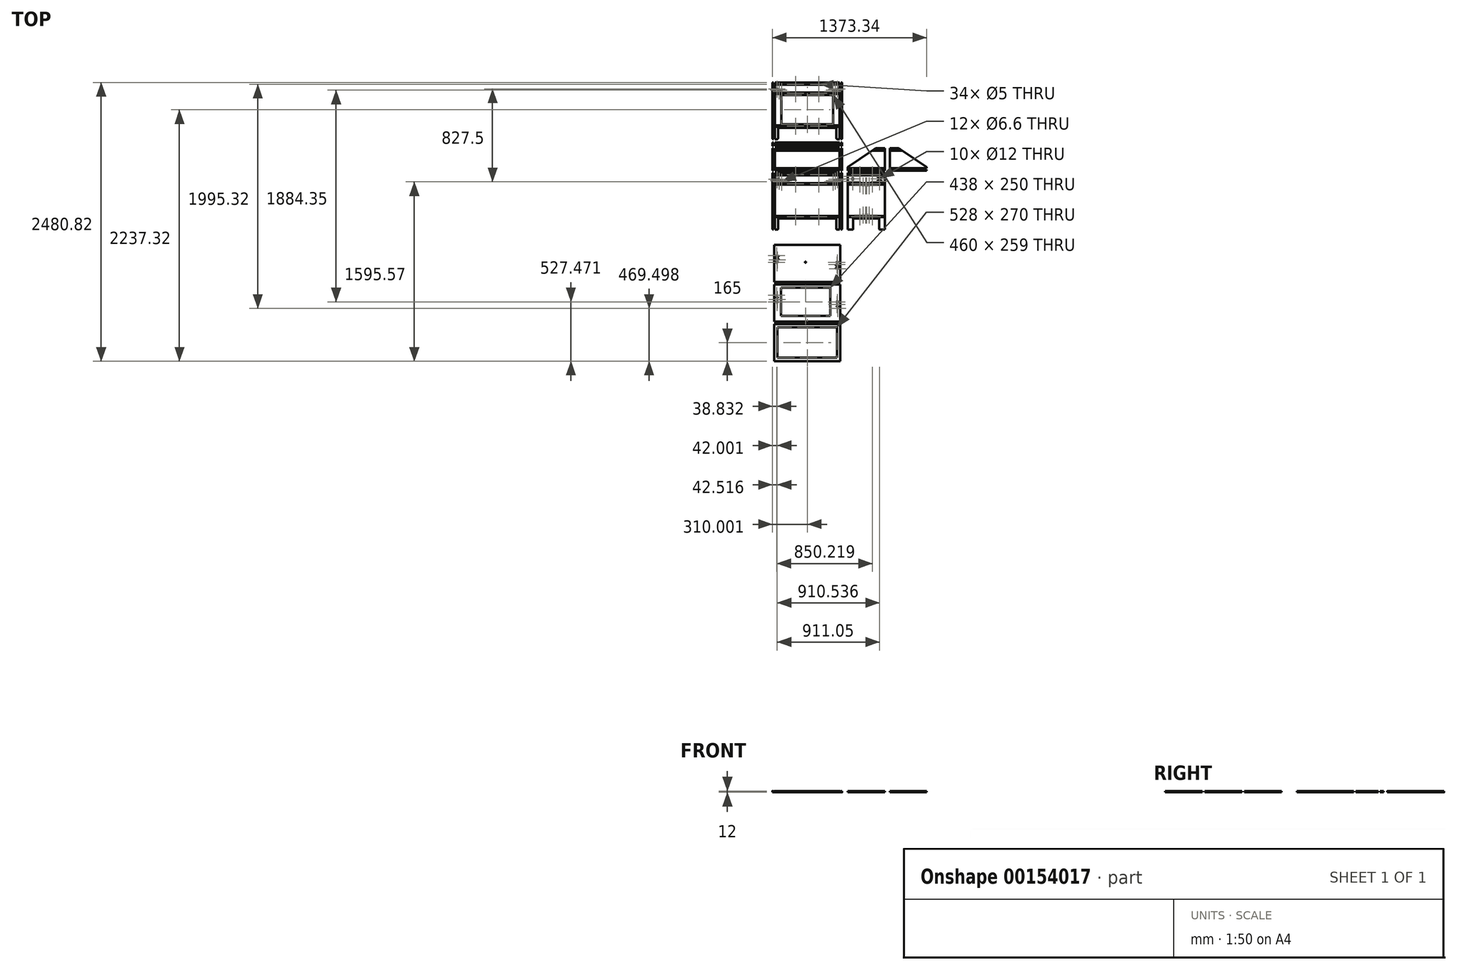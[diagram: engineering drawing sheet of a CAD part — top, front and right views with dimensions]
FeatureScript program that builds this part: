
annotation { "Feature Type Name" : "Feature", "Feature Type Description" : "" }
export const myFeature = defineFeature(function(context is Context, id is Id, definition is map)
    precondition{}
    {
        {
            var Q0;
            Q0=qCreatedBy(makeId("Top.planeOp"),FACE);
            var sketch = newSketch(context, id + "F0", { "sketchPlane" : qUnion([Q0])});
            skLineSegment(sketch, "E0.bottom", {"start": v(-158.16, 0) * mm, "end": v(461.84, 0) * mm, "construction": true});
            skLineSegment(sketch, "E0.left", {"start": v(-158.16, 0) * mm, "end": v(-158.16, 505) * mm});
            skLineSegment(sketch, "E0.right", {"start": v(461.84, 0) * mm, "end": v(461.84, 505) * mm});
            skLineSegment(sketch, "E1", {"start": v(-158.16, 0) * mm, "end": v(-108.16, 0) * mm});
            skLineSegment(sketch, "E2", {"start": v(-108.16, 0) * mm, "end": v(-108.16, 100) * mm});
            skLineSegment(sketch, "E3", {"start": v(-108.16, 100) * mm, "end": v(411.84, 100) * mm});
            skLineSegment(sketch, "E4", {"start": v(411.84, 100) * mm, "end": v(411.84, 0) * mm});
            skLineSegment(sketch, "E5", {"start": v(411.84, 0) * mm, "end": v(461.84, 0) * mm});
            skLineSegment(sketch, "E6", {"start": v(-1603.84, 505) * mm, "end": v(2199.75, 505) * mm, "construction": true});
            skLineSegment(sketch, "E7", {"start": v(-1603.84, 0) * mm, "end": v(2199.75, 0) * mm, "construction": true});
            skLineSegment(sketch, "E8", {"start": v(-158.16, -1362.13) * mm, "end": v(-158.16, 1728.44) * mm, "construction": true});
            skLineSegment(sketch, "E9", {"start": v(461.84, -1362.13) * mm, "end": v(461.84, 1728.44) * mm, "construction": true});
            skLineSegment(sketch, "E10", {"start": v(-158.16, -1362.13) * mm, "end": v(461.84, -1362.13) * mm, "construction": true});
            skLineSegment(sketch, "E11", {"start": v(-1603.84, 505) * mm, "end": v(-1603.84, 0) * mm, "construction": true});
            skLineSegment(sketch, "E12", {"start": v(2199.75, 505) * mm, "end": v(2199.75, 0) * mm, "construction": true});
            skLineSegment(sketch, "E13", {"start": v(461.84, 1728.44) * mm, "end": v(-158.16, 1728.44) * mm, "construction": true});
            skLineSegment(sketch, "E14", {"start": v(510.9, 0) * mm, "end": v(510.9, 505) * mm});
            skLineSegment(sketch, "E15", {"start": v(510.9, 505) * mm, "end": v(840.9, 505) * mm});
            skLineSegment(sketch, "E16", {"start": v(840.9, 505) * mm, "end": v(840.9, 0) * mm});
            skLineSegment(sketch, "E17", {"start": v(840.9, 0) * mm, "end": v(790.9, 0) * mm});
            skLineSegment(sketch, "E18", {"start": v(790.9, 0) * mm, "end": v(790.9, 100) * mm});
            skLineSegment(sketch, "E19", {"start": v(790.9, 100) * mm, "end": v(560.9, 100) * mm});
            skLineSegment(sketch, "E20", {"start": v(560.9, 100) * mm, "end": v(560.9, 0) * mm});
            skLineSegment(sketch, "E21", {"start": v(560.9, 0) * mm, "end": v(510.9, 0) * mm});
            skLineSegment(sketch, "E22.bottom", {"start": v(461.84, 505) * mm, "end": v(451.84, 505) * mm, "construction": true});
            skLineSegment(sketch, "E22.top", {"start": v(461.84, -23.84) * mm, "end": v(451.84, -23.84) * mm, "construction": true});
            skLineSegment(sketch, "E22.left", {"start": v(461.84, 505) * mm, "end": v(461.84, -23.84) * mm, "construction": true});
            skLineSegment(sketch, "E22.right", {"start": v(451.84, 505) * mm, "end": v(451.84, -23.84) * mm, "construction": true});
            skLineSegment(sketch, "E23.bottom", {"start": v(451.84, 505) * mm, "end": v(439.84, 505) * mm, "construction": true});
            skLineSegment(sketch, "E23.top", {"start": v(451.84, -23.84) * mm, "end": v(439.84, -23.84) * mm, "construction": true});
            skLineSegment(sketch, "E23.right", {"start": v(439.84, 505) * mm, "end": v(439.84, -23.84) * mm, "construction": true});
            skLineSegment(sketch, "E24.bottom", {"start": v(-158.16, 505) * mm, "end": v(-148.16, 505) * mm, "construction": true});
            skLineSegment(sketch, "E24.top", {"start": v(-158.16, -23.84) * mm, "end": v(-148.16, -23.84) * mm, "construction": true});
            skLineSegment(sketch, "E24.left", {"start": v(-158.16, 505) * mm, "end": v(-158.16, -23.84) * mm, "construction": true});
            skLineSegment(sketch, "E24.right", {"start": v(-148.16, 505) * mm, "end": v(-148.16, -23.84) * mm, "construction": true});
            skLineSegment(sketch, "E25.bottom", {"start": v(-148.16, 505) * mm, "end": v(-136.16, 505) * mm, "construction": true});
            skLineSegment(sketch, "E25.top", {"start": v(-148.16, -23.84) * mm, "end": v(-136.16, -23.84) * mm, "construction": true});
            skLineSegment(sketch, "E25.right", {"start": v(-136.16, 505) * mm, "end": v(-136.16, -23.84) * mm, "construction": true});
            skLineSegment(sketch, "E26.bottom", {"start": v(-148.16, 505) * mm, "end": v(-136.16, 505) * mm});
            skLineSegment(sketch, "E26.top", {"start": v(-148.16, 0) * mm, "end": v(-136.16, 0) * mm});
            skLineSegment(sketch, "E26.left", {"start": v(-148.16, 505) * mm, "end": v(-148.16, 0) * mm});
            skLineSegment(sketch, "E26.right", {"start": v(-136.16, 505) * mm, "end": v(-136.16, 0) * mm});
            skLineSegment(sketch, "E27.bottom", {"start": v(439.84, 505) * mm, "end": v(451.84, 505) * mm});
            skLineSegment(sketch, "E27.top", {"start": v(439.84, 0) * mm, "end": v(451.84, 0) * mm});
            skLineSegment(sketch, "E27.left", {"start": v(439.84, 505) * mm, "end": v(439.84, 0) * mm});
            skLineSegment(sketch, "E27.right", {"start": v(451.84, 505) * mm, "end": v(451.84, 0) * mm});
            skLineSegment(sketch, "E28", {"start": v(-158.16, 805) * mm, "end": v(-158.16, 1310) * mm});
            skLineSegment(sketch, "E29", {"start": v(-158.16, 1310) * mm, "end": v(461.84, 1310) * mm});
            skLineSegment(sketch, "E30", {"start": v(461.84, 1310) * mm, "end": v(461.84, 805) * mm});
            skLineSegment(sketch, "E31", {"start": v(461.84, 805) * mm, "end": v(411.84, 805) * mm});
            skLineSegment(sketch, "E32", {"start": v(411.84, 805) * mm, "end": v(411.84, 905) * mm});
            skLineSegment(sketch, "E33", {"start": v(411.84, 905) * mm, "end": v(-108.16, 905) * mm});
            skLineSegment(sketch, "E34", {"start": v(-108.16, 905) * mm, "end": v(-108.16, 805) * mm});
            skLineSegment(sketch, "E35", {"start": v(-108.16, 805) * mm, "end": v(-158.16, 805) * mm});
            skLineSegment(sketch, "E36.bottom", {"start": v(-78.16, 1196) * mm, "end": v(381.84, 1196) * mm});
            skLineSegment(sketch, "E36.top", {"start": v(-78.16, 937) * mm, "end": v(381.84, 937) * mm});
            skLineSegment(sketch, "E36.left", {"start": v(-78.16, 1196) * mm, "end": v(-78.16, 937) * mm});
            skLineSegment(sketch, "E36.right", {"start": v(381.84, 1196) * mm, "end": v(381.84, 937) * mm});
            skLineSegment(sketch, "E37.bottom", {"start": v(-78.16, 1278) * mm, "end": v(381.84, 1278) * mm});
            skLineSegment(sketch, "E37.top", {"start": v(-78.16, 1228) * mm, "end": v(381.84, 1228) * mm});
            skLineSegment(sketch, "E37.left", {"start": v(-78.16, 1278) * mm, "end": v(-78.16, 1228) * mm});
            skLineSegment(sketch, "E37.right", {"start": v(381.84, 1278) * mm, "end": v(381.84, 1228) * mm});
            skLineSegment(sketch, "E38", {"start": v(-78.16, 1066.5) * mm, "end": v(-158.16, 1066.5) * mm, "construction": true});
            skLineSegment(sketch, "E39", {"start": v(-78.16, 1253) * mm, "end": v(-158.16, 1253) * mm, "construction": true});
            skLineSegment(sketch, "E40", {"start": v(381.84, 1253) * mm, "end": v(461.84, 1253) * mm, "construction": true});
            skLineSegment(sketch, "E41", {"start": v(381.84, 1066.5) * mm, "end": v(461.84, 1066.5) * mm, "construction": true});
            skLineSegment(sketch, "E42", {"start": v(151.84, 1278) * mm, "end": v(151.84, 1310) * mm, "construction": true});
            skLineSegment(sketch, "E43", {"start": v(151.84, 1228) * mm, "end": v(151.84, 1196) * mm, "construction": true});
            skLineSegment(sketch, "E44", {"start": v(151.84, 937) * mm, "end": v(151.84, 905) * mm, "construction": true});
            skLineSegment(sketch, "E45", {"start": v(-148.16, 505) * mm, "end": v(-148.16, 1310) * mm, "construction": true});
            skLineSegment(sketch, "E46", {"start": v(-136.16, 505) * mm, "end": v(-136.16, 1310) * mm, "construction": true});
            skLineSegment(sketch, "E47", {"start": v(439.84, 505) * mm, "end": v(439.84, 1310) * mm, "construction": true});
            skLineSegment(sketch, "E48", {"start": v(451.84, 505) * mm, "end": v(451.84, 1310) * mm, "construction": true});
            skLineSegment(sketch, "E49.bottom", {"start": v(-148.16, 1310) * mm, "end": v(-136.16, 1310) * mm});
            skLineSegment(sketch, "E49.top", {"start": v(-148.16, 805) * mm, "end": v(-136.16, 805) * mm});
            skLineSegment(sketch, "E49.left", {"start": v(-148.16, 1310) * mm, "end": v(-148.16, 805) * mm});
            skLineSegment(sketch, "E49.right", {"start": v(-136.16, 1310) * mm, "end": v(-136.16, 805) * mm});
            skLineSegment(sketch, "E50.bottom", {"start": v(439.84, 1310) * mm, "end": v(451.84, 1310) * mm});
            skLineSegment(sketch, "E50.top", {"start": v(439.84, 805) * mm, "end": v(451.84, 805) * mm});
            skLineSegment(sketch, "E50.left", {"start": v(439.84, 1310) * mm, "end": v(439.84, 805) * mm});
            skLineSegment(sketch, "E50.right", {"start": v(451.84, 1310) * mm, "end": v(451.84, 805) * mm});
            skLineSegment(sketch, "E51.bottom", {"start": v(-126.62, 1310) * mm, "end": v(-158.16, 1310) * mm, "construction": true});
            skLineSegment(sketch, "E51.top", {"start": v(-126.62, 1300) * mm, "end": v(-158.16, 1300) * mm, "construction": true});
            skLineSegment(sketch, "E51.left", {"start": v(-158.16, 1310) * mm, "end": v(-158.16, 1300) * mm, "construction": true});
            skLineSegment(sketch, "E51.right", {"start": v(-126.62, 1310) * mm, "end": v(-126.62, 1300) * mm, "construction": true});
            skLineSegment(sketch, "E52.bottom", {"start": v(-158.16, 1300) * mm, "end": v(-126.62, 1300) * mm, "construction": true});
            skLineSegment(sketch, "E52.top", {"start": v(-158.16, 1288) * mm, "end": v(-126.62, 1288) * mm, "construction": true});
            skLineSegment(sketch, "E52.left", {"start": v(-126.62, 1300) * mm, "end": v(-126.62, 1288) * mm, "construction": true});
            skLineSegment(sketch, "E52.right", {"start": v(-158.16, 1300) * mm, "end": v(-158.16, 1288) * mm, "construction": true});
            skLineSegment(sketch, "E53.bottom", {"start": v(-126.62, 1228) * mm, "end": v(-158.16, 1228) * mm, "construction": true});
            skLineSegment(sketch, "E53.top", {"start": v(-126.62, 1218) * mm, "end": v(-158.16, 1218) * mm, "construction": true});
            skLineSegment(sketch, "E53.left", {"start": v(-158.16, 1228) * mm, "end": v(-158.16, 1218) * mm, "construction": true});
            skLineSegment(sketch, "E53.right", {"start": v(-126.62, 1228) * mm, "end": v(-126.62, 1218) * mm, "construction": true});
            skLineSegment(sketch, "E54.bottom", {"start": v(-158.16, 1218) * mm, "end": v(-126.62, 1218) * mm, "construction": true});
            skLineSegment(sketch, "E54.top", {"start": v(-158.16, 1206) * mm, "end": v(-126.62, 1206) * mm, "construction": true});
            skLineSegment(sketch, "E54.left", {"start": v(-126.62, 1218) * mm, "end": v(-126.62, 1206) * mm, "construction": true});
            skLineSegment(sketch, "E54.right", {"start": v(-158.16, 1218) * mm, "end": v(-158.16, 1206) * mm, "construction": true});
            skLineSegment(sketch, "E55.bottom", {"start": v(-126.62, 937) * mm, "end": v(-158.16, 937) * mm, "construction": true});
            skLineSegment(sketch, "E55.top", {"start": v(-126.62, 927) * mm, "end": v(-158.16, 927) * mm, "construction": true});
            skLineSegment(sketch, "E55.left", {"start": v(-158.16, 937) * mm, "end": v(-158.16, 927) * mm, "construction": true});
            skLineSegment(sketch, "E55.right", {"start": v(-126.62, 937) * mm, "end": v(-126.62, 927) * mm, "construction": true});
            skLineSegment(sketch, "E56.bottom", {"start": v(-158.16, 927) * mm, "end": v(-126.62, 927) * mm, "construction": true});
            skLineSegment(sketch, "E56.top", {"start": v(-158.16, 915) * mm, "end": v(-126.62, 915) * mm, "construction": true});
            skLineSegment(sketch, "E56.left", {"start": v(-126.62, 927) * mm, "end": v(-126.62, 915) * mm, "construction": true});
            skLineSegment(sketch, "E56.right", {"start": v(-158.16, 927) * mm, "end": v(-158.16, 915) * mm, "construction": true});
            skLineSegment(sketch, "E57", {"start": v(-158.16, 1228) * mm, "end": v(-78.16, 1228) * mm, "construction": true});
            skLineSegment(sketch, "E58", {"start": v(-158.16, 937) * mm, "end": v(-78.16, 937) * mm, "construction": true});
            skLineSegment(sketch, "E59.bottom", {"start": v(-136.16, 1310) * mm, "end": v(-142.16, 1310) * mm, "construction": true});
            skLineSegment(sketch, "E59.top", {"start": v(-136.16, 990.33) * mm, "end": v(-142.16, 990.33) * mm, "construction": true});
            skLineSegment(sketch, "E59.left", {"start": v(-136.16, 990.33) * mm, "end": v(-136.16, 1310) * mm, "construction": true});
            skLineSegment(sketch, "E59.right", {"start": v(-142.16, 990.33) * mm, "end": v(-142.16, 1310) * mm, "construction": true});
            skLineSegment(sketch, "E60.bottom", {"start": v(439.84, 1310) * mm, "end": v(445.84, 1310) * mm, "construction": true});
            skLineSegment(sketch, "E60.top", {"start": v(439.84, 990.33) * mm, "end": v(445.84, 990.33) * mm, "construction": true});
            skLineSegment(sketch, "E60.left", {"start": v(439.84, 990.33) * mm, "end": v(439.84, 1310) * mm, "construction": true});
            skLineSegment(sketch, "E60.right", {"start": v(445.84, 990.33) * mm, "end": v(445.84, 1310) * mm, "construction": true});
            skLineSegment(sketch, "E61", {"start": v(-142.16, 1310) * mm, "end": v(-142.16, -1362.13) * mm, "construction": true});
            skLineSegment(sketch, "E62", {"start": v(445.84, 1310) * mm, "end": v(445.84, -1362.13) * mm, "construction": true});
            skLineSegment(sketch, "E63", {"start": v(-158.16, 1300) * mm, "end": v(445.84, 1300) * mm, "construction": true});
            skLineSegment(sketch, "E64", {"start": v(-158.16, 1288) * mm, "end": v(445.84, 1288) * mm, "construction": true});
            skLineSegment(sketch, "E65", {"start": v(-158.16, 1218) * mm, "end": v(445.84, 1218) * mm, "construction": true});
            skLineSegment(sketch, "E66", {"start": v(-158.16, 1206) * mm, "end": v(445.84, 1206) * mm, "construction": true});
            skLineSegment(sketch, "E67", {"start": v(-158.16, 927) * mm, "end": v(445.84, 927) * mm, "construction": true});
            skLineSegment(sketch, "E68", {"start": v(-158.16, 915) * mm, "end": v(445.84, 915) * mm, "construction": true});
            skLineSegment(sketch, "E69.bottom", {"start": v(-142.16, 927) * mm, "end": v(445.84, 927) * mm});
            skLineSegment(sketch, "E69.top", {"start": v(-142.16, 915) * mm, "end": v(445.84, 915) * mm});
            skLineSegment(sketch, "E69.left", {"start": v(-142.16, 927) * mm, "end": v(-142.16, 915) * mm});
            skLineSegment(sketch, "E69.right", {"start": v(445.84, 927) * mm, "end": v(445.84, 915) * mm});
            skLineSegment(sketch, "E70.bottom", {"start": v(-142.16, 1300) * mm, "end": v(445.84, 1300) * mm});
            skLineSegment(sketch, "E70.top", {"start": v(-142.16, 1288) * mm, "end": v(445.84, 1288) * mm});
            skLineSegment(sketch, "E70.left", {"start": v(-142.16, 1300) * mm, "end": v(-142.16, 1288) * mm});
            skLineSegment(sketch, "E70.right", {"start": v(445.84, 1300) * mm, "end": v(445.84, 1288) * mm});
            skLineSegment(sketch, "E71.bottom", {"start": v(-142.16, 1218) * mm, "end": v(445.84, 1218) * mm});
            skLineSegment(sketch, "E71.top", {"start": v(-142.16, 1206) * mm, "end": v(445.84, 1206) * mm});
            skLineSegment(sketch, "E71.left", {"start": v(-142.16, 1218) * mm, "end": v(-142.16, 1206) * mm});
            skLineSegment(sketch, "E71.right", {"start": v(445.84, 1218) * mm, "end": v(445.84, 1206) * mm});
            skLineSegment(sketch, "E72", {"start": v(-126.62, 1310) * mm, "end": v(-143.96, 1310) * mm, "construction": true});
            skLineSegment(sketch, "E73", {"start": v(-143.96, 1310) * mm, "end": v(-143.96, 1218) * mm, "construction": true});
            skLineSegment(sketch, "E74", {"start": v(-143.96, 1218) * mm, "end": v(-126.62, 1218) * mm, "construction": true});
            skLineSegment(sketch, "E75", {"start": v(-158.16, 505) * mm, "end": v(-174.33, 505) * mm, "construction": true});
            skLineSegment(sketch, "E76", {"start": v(-174.33, 505) * mm, "end": v(-174.33, 495) * mm, "construction": true});
            skLineSegment(sketch, "E77", {"start": v(-174.33, 505) * mm, "end": v(-182.9, 505) * mm, "construction": true});
            skLineSegment(sketch, "E78", {"start": v(-182.9, 505) * mm, "end": v(-182.9, 413) * mm, "construction": true});
            skLineSegment(sketch, "E79", {"start": v(-143.96, 1310) * mm, "end": v(-154.94, 1310) * mm, "construction": true});
            skLineSegment(sketch, "E80", {"start": v(-154.94, 1310) * mm, "end": v(-154.94, 927) * mm, "construction": true});
            skLineSegment(sketch, "E81", {"start": v(-154.94, 927) * mm, "end": v(-126.62, 927) * mm, "construction": true});
            skLineSegment(sketch, "E82", {"start": v(-158.16, 505) * mm, "end": v(-192.87, 505) * mm, "construction": true});
            skLineSegment(sketch, "E83", {"start": v(-192.87, 505) * mm, "end": v(-192.87, 122) * mm, "construction": true});
            skLineSegment(sketch, "E84.bottom", {"start": v(-174.33, 495) * mm, "end": v(445.84, 495) * mm, "construction": true});
            skLineSegment(sketch, "E84.top", {"start": v(-174.33, 483) * mm, "end": v(445.84, 483) * mm, "construction": true});
            skLineSegment(sketch, "E84.left", {"start": v(-174.33, 495) * mm, "end": v(-174.33, 483) * mm, "construction": true});
            skLineSegment(sketch, "E84.right", {"start": v(445.84, 495) * mm, "end": v(445.84, 483) * mm, "construction": true});
            skLineSegment(sketch, "E85.bottom", {"start": v(-182.9, 413) * mm, "end": v(445.84, 413) * mm, "construction": true});
            skLineSegment(sketch, "E85.top", {"start": v(-182.9, 401) * mm, "end": v(445.84, 401) * mm, "construction": true});
            skLineSegment(sketch, "E85.left", {"start": v(-182.9, 413) * mm, "end": v(-182.9, 401) * mm, "construction": true});
            skLineSegment(sketch, "E85.right", {"start": v(445.84, 413) * mm, "end": v(445.84, 401) * mm, "construction": true});
            skLineSegment(sketch, "E86.bottom", {"start": v(-192.87, 122) * mm, "end": v(445.84, 122) * mm, "construction": true});
            skLineSegment(sketch, "E86.top", {"start": v(-192.87, 110) * mm, "end": v(445.84, 110) * mm, "construction": true});
            skLineSegment(sketch, "E86.left", {"start": v(-192.87, 122) * mm, "end": v(-192.87, 110) * mm, "construction": true});
            skLineSegment(sketch, "E86.right", {"start": v(445.84, 122) * mm, "end": v(445.84, 110) * mm, "construction": true});
            skLineSegment(sketch, "E87.bottom", {"start": v(-142.16, 495) * mm, "end": v(445.84, 495) * mm});
            skLineSegment(sketch, "E87.top", {"start": v(-142.16, 483) * mm, "end": v(445.84, 483) * mm});
            skLineSegment(sketch, "E87.left", {"start": v(-142.16, 495) * mm, "end": v(-142.16, 483) * mm});
            skLineSegment(sketch, "E87.right", {"start": v(445.84, 495) * mm, "end": v(445.84, 483) * mm});
            skLineSegment(sketch, "E88.bottom", {"start": v(-142.16, 413) * mm, "end": v(445.84, 413) * mm});
            skLineSegment(sketch, "E88.top", {"start": v(-142.16, 401) * mm, "end": v(445.84, 401) * mm});
            skLineSegment(sketch, "E88.left", {"start": v(-142.16, 413) * mm, "end": v(-142.16, 401) * mm});
            skLineSegment(sketch, "E88.right", {"start": v(445.84, 413) * mm, "end": v(445.84, 401) * mm});
            skLineSegment(sketch, "E89.bottom", {"start": v(-142.16, 122) * mm, "end": v(445.84, 122) * mm});
            skLineSegment(sketch, "E89.top", {"start": v(-142.16, 110) * mm, "end": v(445.84, 110) * mm});
            skLineSegment(sketch, "E89.left", {"start": v(-142.16, 122) * mm, "end": v(-142.16, 110) * mm});
            skLineSegment(sketch, "E89.right", {"start": v(445.84, 122) * mm, "end": v(445.84, 110) * mm});
            skLineSegment(sketch, "E90", {"start": v(445.84, 495) * mm, "end": v(840.9, 495) * mm, "construction": true});
            skLineSegment(sketch, "E91", {"start": v(445.84, 483) * mm, "end": v(840.9, 483) * mm, "construction": true});
            skLineSegment(sketch, "E92", {"start": v(445.84, 413) * mm, "end": v(840.9, 413) * mm, "construction": true});
            skLineSegment(sketch, "E93", {"start": v(445.84, 401) * mm, "end": v(840.9, 401) * mm, "construction": true});
            skLineSegment(sketch, "E94", {"start": v(445.84, 122) * mm, "end": v(840.9, 122) * mm, "construction": true});
            skLineSegment(sketch, "E95", {"start": v(445.84, 110) * mm, "end": v(840.9, 110) * mm, "construction": true});
            skLineSegment(sketch, "E96.right", {"start": v(840.9, 505) * mm, "end": v(840.9, 110) * mm, "construction": true});
            skLineSegment(sketch, "E97.bottom", {"start": v(840.9, 495) * mm, "end": v(510.9, 495) * mm});
            skLineSegment(sketch, "E97.top", {"start": v(840.9, 483) * mm, "end": v(510.9, 483) * mm});
            skLineSegment(sketch, "E97.left", {"start": v(840.9, 495) * mm, "end": v(840.9, 483) * mm});
            skLineSegment(sketch, "E98.bottom", {"start": v(840.9, 122) * mm, "end": v(510.9, 122) * mm});
            skLineSegment(sketch, "E98.top", {"start": v(840.9, 110) * mm, "end": v(510.9, 110) * mm});
            skLineSegment(sketch, "E99.bottom", {"start": v(840.9, 413) * mm, "end": v(510.9, 413) * mm});
            skLineSegment(sketch, "E99.top", {"start": v(840.9, 401) * mm, "end": v(510.9, 401) * mm});
            skLineSegment(sketch, "E99.left", {"start": v(840.9, 413) * mm, "end": v(840.9, 401) * mm});
            skLineSegment(sketch, "E99.right", {"start": v(510.9, 413) * mm, "end": v(510.9, 401) * mm});
            skLineSegment(sketch, "E100.bottom", {"start": v(-142.16, -135.27) * mm, "end": v(325.84, -135.27) * mm, "construction": true});
            skLineSegment(sketch, "E100.top", {"start": v(-142.16, -465.27) * mm, "end": v(325.84, -465.27) * mm, "construction": true});
            skLineSegment(sketch, "E100.left", {"start": v(-142.16, -135.27) * mm, "end": v(-142.16, -465.27) * mm, "construction": true});
            skLineSegment(sketch, "E100.right", {"start": v(325.84, -135.27) * mm, "end": v(325.84, -465.27) * mm, "construction": true});
            skLineSegment(sketch, "E101.bottom", {"start": v(-142.16, -135.27) * mm, "end": v(445.84, -135.27) * mm});
            skLineSegment(sketch, "E101.top", {"start": v(-142.16, -465.27) * mm, "end": v(445.84, -465.27) * mm});
            skLineSegment(sketch, "E101.left", {"start": v(-142.16, -135.27) * mm, "end": v(-142.16, -465.27) * mm});
            skLineSegment(sketch, "E101.right", {"start": v(445.84, -135.27) * mm, "end": v(445.84, -465.27) * mm});
            skLineSegment(sketch, "E102.bottom", {"start": v(-142.16, -488.35) * mm, "end": v(325.84, -488.35) * mm, "construction": true});
            skLineSegment(sketch, "E102.top", {"start": v(-142.16, -818.35) * mm, "end": v(325.84, -818.35) * mm, "construction": true});
            skLineSegment(sketch, "E102.left", {"start": v(-142.16, -488.35) * mm, "end": v(-142.16, -818.35) * mm, "construction": true});
            skLineSegment(sketch, "E102.right", {"start": v(325.84, -488.35) * mm, "end": v(325.84, -818.35) * mm, "construction": true});
            skLineSegment(sketch, "E103.bottom", {"start": v(-142.16, -488.35) * mm, "end": v(445.84, -488.35) * mm});
            skLineSegment(sketch, "E103.top", {"start": v(-142.16, -818.35) * mm, "end": v(445.84, -818.35) * mm});
            skLineSegment(sketch, "E103.left", {"start": v(-142.16, -488.35) * mm, "end": v(-142.16, -818.35) * mm});
            skLineSegment(sketch, "E103.right", {"start": v(445.84, -488.35) * mm, "end": v(445.84, -818.35) * mm});
            skLineSegment(sketch, "E104.bottom", {"start": v(-82.16, -518.35) * mm, "end": v(355.84, -518.35) * mm});
            skLineSegment(sketch, "E104.top", {"start": v(-82.16, -768.35) * mm, "end": v(355.84, -768.35) * mm});
            skLineSegment(sketch, "E104.left", {"start": v(-82.16, -518.35) * mm, "end": v(-82.16, -768.35) * mm});
            skLineSegment(sketch, "E104.right", {"start": v(355.84, -518.35) * mm, "end": v(355.84, -768.35) * mm});
            skLineSegment(sketch, "E105", {"start": v(-142.16, -643.35) * mm, "end": v(-82.16, -643.35) * mm, "construction": true});
            skLineSegment(sketch, "E106", {"start": v(151.84, -488.35) * mm, "end": v(151.84, -518.35) * mm, "construction": true});
            skLineSegment(sketch, "E107", {"start": v(445.84, -643.35) * mm, "end": v(355.84, -643.35) * mm, "construction": true});
            skLineSegment(sketch, "E108", {"start": v(91.84, -818.35) * mm, "end": v(91.84, -768.35) * mm, "construction": true});
            skLineSegment(sketch, "E109", {"start": v(-82.16, -643.35) * mm, "end": v(136.84, -643.35) * mm, "construction": true});
            skLineSegment(sketch, "E110", {"start": v(136.84, -643.35) * mm, "end": v(136.84, -518.35) * mm, "construction": true});
            skLineSegment(sketch, "E111", {"start": v(136.84, -518.35) * mm, "end": v(136.84, -488.35) * mm, "construction": true});
            skLineSegment(sketch, "E112", {"start": v(136.84, -488.35) * mm, "end": v(136.84, -290.27) * mm, "construction": true});
            skLineSegment(sketch, "E113", {"start": v(136.84, -290.27) * mm, "end": v(136.84, -165.27) * mm, "construction": true});
            skLineSegment(sketch, "E114", {"start": v(136.84, -165.27) * mm, "end": v(136.84, -135.27) * mm, "construction": true});
            skCircle(sketch, "E115", {"center": v(136.84, -290.27) * mm, "radius": 4.79 * mm});
            skLineSegment(sketch, "E116.bottom", {"start": v(-142.16, -840.82) * mm, "end": v(445.84, -840.82) * mm});
            skLineSegment(sketch, "E116.top", {"start": v(-142.16, -1170.82) * mm, "end": v(445.84, -1170.82) * mm});
            skLineSegment(sketch, "E116.left", {"start": v(-142.16, -840.82) * mm, "end": v(-142.16, -1170.82) * mm});
            skLineSegment(sketch, "E116.right", {"start": v(445.84, -840.82) * mm, "end": v(445.84, -1170.82) * mm});
            skLineSegment(sketch, "E117.bottom", {"start": v(-112.16, -870.82) * mm, "end": v(415.84, -870.82) * mm});
            skLineSegment(sketch, "E117.top", {"start": v(-112.16, -1140.82) * mm, "end": v(415.84, -1140.82) * mm});
            skLineSegment(sketch, "E117.left", {"start": v(-112.16, -870.82) * mm, "end": v(-112.16, -1140.82) * mm});
            skLineSegment(sketch, "E117.right", {"start": v(415.84, -870.82) * mm, "end": v(415.84, -1140.82) * mm});
            skLineSegment(sketch, "E118", {"start": v(151.84, -840.82) * mm, "end": v(151.84, -870.82) * mm, "construction": true});
            skLineSegment(sketch, "E119", {"start": v(-112.16, -1005.82) * mm, "end": v(-142.16, -1005.82) * mm, "construction": true});
            skLineSegment(sketch, "E120", {"start": v(151.84, -1140.82) * mm, "end": v(151.84, -1170.82) * mm, "construction": true});
            skLineSegment(sketch, "E121", {"start": v(415.84, -1005.82) * mm, "end": v(445.84, -1005.82) * mm, "construction": true});
            skLineSegment(sketch, "E122", {"start": v(-269.74, 505) * mm, "end": v(-269.74, 725) * mm, "construction": true});
            skLineSegment(sketch, "E123", {"start": v(-269.74, 725) * mm, "end": v(2199.75, 725) * mm, "construction": true});
            skLineSegment(sketch, "E124.bottom", {"start": v(-158.16, 505) * mm, "end": v(461.84, 505) * mm});
            skLineSegment(sketch, "E125", {"start": v(-269.74, 525) * mm, "end": v(2199.75, 525) * mm, "construction": true});
            skLineSegment(sketch, "E126.bottom", {"start": v(-158.16, 725) * mm, "end": v(461.84, 725) * mm});
            skLineSegment(sketch, "E126.top", {"start": v(-158.16, 525) * mm, "end": v(461.84, 525) * mm});
            skLineSegment(sketch, "E126.left", {"start": v(-158.16, 725) * mm, "end": v(-158.16, 525) * mm});
            skLineSegment(sketch, "E126.right", {"start": v(461.84, 725) * mm, "end": v(461.84, 525) * mm});
            skLineSegment(sketch, "E127", {"start": v(2199.75, 725) * mm, "end": v(2199.75, 525) * mm, "construction": true});
            skLineSegment(sketch, "E128", {"start": v(2199.75, 525) * mm, "end": v(2199.75, 505) * mm, "construction": true});
            skLineSegment(sketch, "E129", {"start": v(510.9, 525) * mm, "end": v(840.9, 525) * mm});
            skLineSegment(sketch, "E130", {"start": v(840.9, 525) * mm, "end": v(840.9, 725) * mm});
            skLineSegment(sketch, "E131", {"start": v(840.9, 725) * mm, "end": v(760.9, 725) * mm});
            skLineSegment(sketch, "E132", {"start": v(760.9, 725) * mm, "end": v(510.9, 557) * mm});
            skLineSegment(sketch, "E133", {"start": v(510.9, 557) * mm, "end": v(510.9, 525) * mm});
            skLineSegment(sketch, "E134", {"start": v(885.18, 525) * mm, "end": v(885.18, 725) * mm});
            skLineSegment(sketch, "E135", {"start": v(885.18, 725) * mm, "end": v(965.18, 725) * mm});
            skLineSegment(sketch, "E136", {"start": v(965.18, 725) * mm, "end": v(1215.18, 557) * mm});
            skLineSegment(sketch, "E137", {"start": v(1215.18, 557) * mm, "end": v(1215.18, 525) * mm});
            skLineSegment(sketch, "E138", {"start": v(1215.18, 525) * mm, "end": v(885.18, 525) * mm});
            skLineSegment(sketch, "E139.bottom", {"start": v(-158.16, 741.8) * mm, "end": v(461.84, 741.8) * mm});
            skLineSegment(sketch, "E139.top", {"start": v(-158.16, 773.8) * mm, "end": v(461.84, 773.8) * mm});
            skLineSegment(sketch, "E139.left", {"start": v(-158.16, 741.8) * mm, "end": v(-158.16, 773.8) * mm});
            skLineSegment(sketch, "E139.right", {"start": v(461.84, 741.8) * mm, "end": v(461.84, 773.8) * mm});
            skLineSegment(sketch, "E140.bottom", {"start": v(439.84, 773.8) * mm, "end": v(451.84, 773.8) * mm});
            skLineSegment(sketch, "E140.top", {"start": v(439.84, 741.8) * mm, "end": v(451.84, 741.8) * mm});
            skLineSegment(sketch, "E140.left", {"start": v(439.84, 773.8) * mm, "end": v(439.84, 741.8) * mm});
            skLineSegment(sketch, "E140.right", {"start": v(451.84, 773.8) * mm, "end": v(451.84, 741.8) * mm});
            skLineSegment(sketch, "E141.bottom", {"start": v(-148.16, 773.8) * mm, "end": v(-136.16, 773.8) * mm});
            skLineSegment(sketch, "E141.top", {"start": v(-148.16, 741.8) * mm, "end": v(-136.16, 741.8) * mm});
            skLineSegment(sketch, "E141.left", {"start": v(-148.16, 773.8) * mm, "end": v(-148.16, 741.8) * mm});
            skLineSegment(sketch, "E141.right", {"start": v(-136.16, 773.8) * mm, "end": v(-136.16, 741.8) * mm});
            skLineSegment(sketch, "E142.bottom", {"start": v(439.84, 525) * mm, "end": v(451.84, 525) * mm});
            skLineSegment(sketch, "E142.top", {"start": v(439.84, 725) * mm, "end": v(451.84, 725) * mm});
            skLineSegment(sketch, "E142.left", {"start": v(439.84, 525) * mm, "end": v(439.84, 725) * mm});
            skLineSegment(sketch, "E142.right", {"start": v(451.84, 525) * mm, "end": v(451.84, 725) * mm});
            skLineSegment(sketch, "E143.bottom", {"start": v(-148.16, 525) * mm, "end": v(-136.16, 525) * mm});
            skLineSegment(sketch, "E143.top", {"start": v(-148.16, 725) * mm, "end": v(-136.16, 725) * mm});
            skLineSegment(sketch, "E143.left", {"start": v(-148.16, 525) * mm, "end": v(-148.16, 725) * mm});
            skLineSegment(sketch, "E143.right", {"start": v(-136.16, 525) * mm, "end": v(-136.16, 725) * mm});
            skLineSegment(sketch, "E144", {"start": v(-174.49, 525) * mm, "end": v(-174.49, 535) * mm, "construction": true});
            skLineSegment(sketch, "E145", {"start": v(-174.49, 535) * mm, "end": v(-174.49, 547) * mm, "construction": true});
            skLineSegment(sketch, "E146", {"start": v(-174.49, 547) * mm, "end": v(-174.49, 557) * mm, "construction": true});
            skLineSegment(sketch, "E147", {"start": v(-174.49, 547) * mm, "end": v(2199.75, 547) * mm, "construction": true});
            skLineSegment(sketch, "E148", {"start": v(-174.49, 535) * mm, "end": v(2199.75, 535) * mm, "construction": true});
            skLineSegment(sketch, "E149", {"start": v(-174.49, 557) * mm, "end": v(2199.75, 557) * mm, "construction": true});
            skLineSegment(sketch, "E150", {"start": v(-158.16, 741.8) * mm, "end": v(-178.05, 741.8) * mm, "construction": true});
            skLineSegment(sketch, "E151", {"start": v(-178.05, 741.8) * mm, "end": v(-178.05, 751.8) * mm, "construction": true});
            skLineSegment(sketch, "E152", {"start": v(-178.05, 751.8) * mm, "end": v(-178.05, 763.8) * mm, "construction": true});
            skLineSegment(sketch, "E153", {"start": v(-178.05, 763.8) * mm, "end": v(-178.05, 773.8) * mm, "construction": true});
            skLineSegment(sketch, "E154", {"start": v(-178.05, 773.8) * mm, "end": v(-158.16, 773.8) * mm, "construction": true});
            skLineSegment(sketch, "E155", {"start": v(-178.05, 763.8) * mm, "end": v(483.16, 763.8) * mm, "construction": true});
            skLineSegment(sketch, "E156", {"start": v(-178.05, 751.8) * mm, "end": v(483.16, 751.8) * mm, "construction": true});
            skPoint(sketch, "E157.oppositeSnap0", {"position": v(451.84, 757.8) * mm});
            skLineSegment(sketch, "E157.bottom", {"start": v(-148.16, 763.8) * mm, "end": v(451.84, 763.8) * mm});
            skLineSegment(sketch, "E157.top", {"start": v(-148.16, 751.8) * mm, "end": v(451.84, 751.8) * mm});
            skLineSegment(sketch, "E157.left", {"start": v(-148.16, 763.8) * mm, "end": v(-148.16, 751.8) * mm});
            skLineSegment(sketch, "E157.right", {"start": v(451.84, 763.8) * mm, "end": v(451.84, 751.8) * mm});
            skLineSegment(sketch, "E158.bottom", {"start": v(510.9, 547) * mm, "end": v(840.9, 547) * mm});
            skLineSegment(sketch, "E158.top", {"start": v(510.9, 535) * mm, "end": v(840.9, 535) * mm});
            skLineSegment(sketch, "E158.left", {"start": v(510.9, 547) * mm, "end": v(510.9, 535) * mm});
            skLineSegment(sketch, "E158.right", {"start": v(840.9, 547) * mm, "end": v(840.9, 535) * mm});
            skLineSegment(sketch, "E159.bottom", {"start": v(885.18, 547) * mm, "end": v(1215.18, 547) * mm});
            skLineSegment(sketch, "E159.top", {"start": v(885.18, 535) * mm, "end": v(1215.18, 535) * mm});
            skLineSegment(sketch, "E159.left", {"start": v(885.18, 547) * mm, "end": v(885.18, 535) * mm});
            skLineSegment(sketch, "E159.right", {"start": v(1215.18, 547) * mm, "end": v(1215.18, 535) * mm});
            skLineSegment(sketch, "E160", {"start": v(510.9, 557) * mm, "end": v(510.9, 703) * mm, "construction": true});
            skLineSegment(sketch, "E161", {"start": v(510.9, 703) * mm, "end": v(510.9, 715) * mm, "construction": true});
            skLineSegment(sketch, "E162", {"start": v(510.9, 715) * mm, "end": v(510.9, 725) * mm, "construction": true});
            skLineSegment(sketch, "E163", {"start": v(510.9, 715) * mm, "end": v(2199.75, 715) * mm, "construction": true});
            skLineSegment(sketch, "E164", {"start": v(510.9, 703) * mm, "end": v(2199.75, 703) * mm, "construction": true});
            skLineSegment(sketch, "E165", {"start": v(746.01, 715) * mm, "end": v(840.9, 715) * mm});
            skLineSegment(sketch, "E166", {"start": v(728.15, 703) * mm, "end": v(840.9, 703) * mm});
            skLineSegment(sketch, "E167", {"start": v(885.18, 715) * mm, "end": v(980.06, 715) * mm});
            skLineSegment(sketch, "E168", {"start": v(885.18, 703) * mm, "end": v(997.92, 703) * mm});
            skLineSegment(sketch, "E169", {"start": v(510.9, 715) * mm, "end": v(-148.16, 715) * mm, "construction": true});
            skLineSegment(sketch, "E170", {"start": v(510.9, 703) * mm, "end": v(-148.16, 703) * mm, "construction": true});
            skLineSegment(sketch, "E171.bottom", {"start": v(-148.16, 715) * mm, "end": v(451.84, 715) * mm});
            skLineSegment(sketch, "E171.top", {"start": v(-148.16, 703) * mm, "end": v(451.84, 703) * mm});
            skLineSegment(sketch, "E171.left", {"start": v(-148.16, 715) * mm, "end": v(-148.16, 703) * mm});
            skLineSegment(sketch, "E171.right", {"start": v(451.84, 715) * mm, "end": v(451.84, 703) * mm});
            skLineSegment(sketch, "E172.bottom", {"start": v(-148.16, 535) * mm, "end": v(451.84, 535) * mm});
            skLineSegment(sketch, "E172.top", {"start": v(-148.16, 547) * mm, "end": v(451.84, 547) * mm});
            skLineSegment(sketch, "E172.left", {"start": v(-148.16, 535) * mm, "end": v(-148.16, 547) * mm});
            skLineSegment(sketch, "E172.right", {"start": v(451.84, 535) * mm, "end": v(451.84, 547) * mm});
            skSolve(sketch);
        }
        {
            var Q0;
            {var subQ3=sQuery(id+"F0.wireOp",EDGE,"E49.right");var subQ5=sQuery(id+"F0.wireOp",EDGE,"E71.bottom");var subQ7=makeQuery(id+"F0.imprint","INTERSECT",VERTEX,{"derivedFrom":[subQ3,subQ5]});Q0=makeQuery(id+"F0.imprint","IMPRINT",FACE,{"disambiguationData":[TD([[makeQuery(id+"F0.imprint","IMPRINT",EDGE,{"disambiguationData":[TD([[subQ7,-1.0]])],"derivedFrom":subQ3}),1.0]])]});}
            var Q1;
            {var subQ1=sQuery(id+"F0.wireOp",EDGE,"E97.top");Q1=makeQuery(id+"F0.imprint","IMPRINT",FACE,{"disambiguationData":[TD([[makeQuery(id+"F0.imprint","IMPRINT",EDGE,{"derivedFrom":subQ1}),1.0]])]});}
            var Q2;
            {var subQ2=sQuery(id+"F0.wireOp",EDGE,"E30");Q2=makeQuery(id+"F0.imprint","IMPRINT",FACE,{"disambiguationData":[TD([[makeQuery(id+"F0.imprint","IMPRINT",EDGE,{"derivedFrom":subQ2}),-1.0]])]});}
            var Q3;
            {var subQ1=sQuery(id+"F0.wireOp",EDGE,"E98.bottom");Q3=makeQuery(id+"F0.imprint","IMPRINT",FACE,{"disambiguationData":[TD([[makeQuery(id+"F0.imprint","IMPRINT",EDGE,{"derivedFrom":subQ1}),-1.0]])]});}
            var Q4;
            {var subQ0=sQuery(id+"F0.wireOp",EDGE,"E88.top");var subQ3=sQuery(id+"F0.wireOp",EDGE,"E26.right");var subQ4=makeQuery(id+"F0.imprint","INTERSECT",VERTEX,{"derivedFrom":[subQ3,subQ0]});Q4=makeQuery(id+"F0.imprint","IMPRINT",FACE,{"disambiguationData":[TD([[makeQuery(id+"F0.imprint","IMPRINT",EDGE,{"disambiguationData":[TD([[subQ4,-1.0]])],"derivedFrom":subQ3}),1.0]])]});}
            var Q5;
            Q5=makeQuery(id+"F0.imprint","IMPRINT",FACE,{"disambiguationData":[TD([[makeQuery(id+"F0.imprint","IMPRINT",EDGE,{"derivedFrom":sQuery(id+"F0.wireOp",EDGE,"E99.bottom")}),1.0]])]});
            var Q6;
            {var subQ0=sQuery(id+"F0.wireOp",EDGE,"E69.bottom");var subQ3=sQuery(id+"F0.wireOp",EDGE,"E49.right");var subQ4=makeQuery(id+"F0.imprint","INTERSECT",VERTEX,{"derivedFrom":[subQ3,subQ0]});Q6=makeQuery(id+"F0.imprint","IMPRINT",FACE,{"disambiguationData":[TD([[makeQuery(id+"F0.imprint","IMPRINT",EDGE,{"disambiguationData":[TD([[subQ4,-1.0]])],"derivedFrom":subQ3}),1.0]])]});}
            var Q7;
            Q7=makeQuery(id+"F0.imprint","IMPRINT",FACE,{"disambiguationData":[TD([[makeQuery(id+"F0.imprint","IMPRINT",EDGE,{"derivedFrom":sQuery(id+"F0.wireOp",EDGE,"E37.bottom")}),1.0]])]});
            var Q8;
            {var subQ0=sQuery(id+"F0.wireOp",EDGE,"E87.bottom");var subQ3=sQuery(id+"F0.wireOp",EDGE,"E26.right");var subQ4=makeQuery(id+"F0.imprint","INTERSECT",VERTEX,{"derivedFrom":[subQ3,subQ0]});Q8=makeQuery(id+"F0.imprint","IMPRINT",FACE,{"disambiguationData":[TD([[makeQuery(id+"F0.imprint","IMPRINT",EDGE,{"disambiguationData":[TD([[subQ4,-1.0]])],"derivedFrom":subQ0}),1.0]])]});}
            var Q9;
            {var subQ3=sQuery(id+"F0.wireOp",EDGE,"E17");Q9=makeQuery(id+"F0.imprint","IMPRINT",FACE,{"disambiguationData":[TD([[makeQuery(id+"F0.imprint","IMPRINT",EDGE,{"derivedFrom":subQ3}),-1.0]])]});}
            var Q10;
            {var subQ1=sQuery(id+"F0.wireOp",EDGE,"E98.bottom");Q10=makeQuery(id+"F0.imprint","IMPRINT",FACE,{"disambiguationData":[TD([[makeQuery(id+"F0.imprint","IMPRINT",EDGE,{"derivedFrom":subQ1}),1.0]])]});}
            var Q11;
            {var subQ0=sQuery(id+"F0.wireOp",EDGE,"E49.right");var subQ1=sQuery(id+"F0.wireOp",EDGE,"E70.bottom");var subQ2=makeQuery(id+"F0.imprint","INTERSECT",VERTEX,{"derivedFrom":[subQ0,subQ1]});Q11=makeQuery(id+"F0.imprint","IMPRINT",FACE,{"disambiguationData":[TD([[makeQuery(id+"F0.imprint","IMPRINT",EDGE,{"disambiguationData":[TD([[subQ2,-1.0]])],"derivedFrom":subQ1}),1.0]])]});}
            var Q12;
            {var subQ10=sQuery(id+"F0.wireOp",EDGE,"E2");Q12=makeQuery(id+"F0.imprint","IMPRINT",FACE,{"disambiguationData":[TD([[makeQuery(id+"F0.imprint","IMPRINT",EDGE,{"derivedFrom":subQ10}),1.0]])]});}
            var Q13;
            {var subQ3=sQuery(id+"F0.wireOp",EDGE,"E49.right");var subQ5=sQuery(id+"F0.wireOp",EDGE,"E70.bottom");var subQ7=makeQuery(id+"F0.imprint","INTERSECT",VERTEX,{"derivedFrom":[subQ3,subQ5]});Q13=makeQuery(id+"F0.imprint","IMPRINT",FACE,{"disambiguationData":[TD([[makeQuery(id+"F0.imprint","IMPRINT",EDGE,{"disambiguationData":[TD([[subQ7,-1.0]])],"derivedFrom":subQ3}),1.0]])]});}
            var Q14;
            Q14=makeQuery(id+"F0.imprint","IMPRINT",FACE,{"disambiguationData":[TD([[makeQuery(id+"F0.imprint","IMPRINT",EDGE,{"derivedFrom":sQuery(id+"F0.wireOp",EDGE,"E36.bottom")}),1.0]])]});
            var Q15;
            {var subQ2=sQuery(id+"F0.wireOp",EDGE,"E15");Q15=makeQuery(id+"F0.imprint","IMPRINT",FACE,{"disambiguationData":[TD([[makeQuery(id+"F0.imprint","IMPRINT",EDGE,{"derivedFrom":subQ2}),-1.0]])]});}
            var Q16;
            {var subQ3=sQuery(id+"F0.wireOp",EDGE,"E26.right");var subQ5=sQuery(id+"F0.wireOp",EDGE,"E88.bottom");var subQ7=makeQuery(id+"F0.imprint","INTERSECT",VERTEX,{"derivedFrom":[subQ3,subQ5]});Q16=makeQuery(id+"F0.imprint","IMPRINT",FACE,{"disambiguationData":[TD([[makeQuery(id+"F0.imprint","IMPRINT",EDGE,{"disambiguationData":[TD([[subQ7,-1.0]])],"derivedFrom":subQ3}),1.0]])]});}
            var Q17;
            {var subQ3=sQuery(id+"F0.wireOp",EDGE,"E26.right");var subQ5=sQuery(id+"F0.wireOp",EDGE,"E87.top");var subQ7=makeQuery(id+"F0.imprint","INTERSECT",VERTEX,{"derivedFrom":[subQ3,subQ5]});Q17=makeQuery(id+"F0.imprint","IMPRINT",FACE,{"disambiguationData":[TD([[makeQuery(id+"F0.imprint","IMPRINT",EDGE,{"disambiguationData":[TD([[subQ7,-1.0]])],"derivedFrom":subQ3}),1.0]])]});}
            var Q18;
            {var subQ2=sQuery(id+"F0.wireOp",EDGE,"E0.left");Q18=makeQuery(id+"F0.imprint","IMPRINT",FACE,{"disambiguationData":[TD([[makeQuery(id+"F0.imprint","IMPRINT",EDGE,{"derivedFrom":subQ2}),-1.0]])]});}
            var Q19;
            {var subQ1=sQuery(id+"F0.wireOp",EDGE,"E97.bottom");Q19=makeQuery(id+"F0.imprint","IMPRINT",FACE,{"disambiguationData":[TD([[makeQuery(id+"F0.imprint","IMPRINT",EDGE,{"derivedFrom":subQ1}),1.0]])]});}
            var Q20;
            {var subQ10=sQuery(id+"F0.wireOp",EDGE,"E32");Q20=makeQuery(id+"F0.imprint","IMPRINT",FACE,{"disambiguationData":[TD([[makeQuery(id+"F0.imprint","IMPRINT",EDGE,{"derivedFrom":subQ10}),-1.0]])]});}
            var Q21;
            {var subQ0=sQuery(id+"F0.wireOp",EDGE,"E87.bottom");var subQ3=sQuery(id+"F0.wireOp",EDGE,"E26.right");var subQ4=makeQuery(id+"F0.imprint","INTERSECT",VERTEX,{"derivedFrom":[subQ3,subQ0]});Q21=makeQuery(id+"F0.imprint","IMPRINT",FACE,{"disambiguationData":[TD([[makeQuery(id+"F0.imprint","IMPRINT",EDGE,{"disambiguationData":[TD([[subQ4,-1.0]])],"derivedFrom":subQ3}),1.0]])]});}
            var Q22;
            {var subQ0=sQuery(id+"F0.wireOp",EDGE,"E89.bottom");var subQ3=sQuery(id+"F0.wireOp",EDGE,"E26.right");var subQ4=makeQuery(id+"F0.imprint","INTERSECT",VERTEX,{"derivedFrom":[subQ3,subQ0]});Q22=makeQuery(id+"F0.imprint","IMPRINT",FACE,{"disambiguationData":[TD([[makeQuery(id+"F0.imprint","IMPRINT",EDGE,{"disambiguationData":[TD([[subQ4,-1.0]])],"derivedFrom":subQ3}),1.0]])]});}
            var Q23;
            {var subQ2=sQuery(id+"F0.wireOp",EDGE,"E28");Q23=makeQuery(id+"F0.imprint","IMPRINT",FACE,{"disambiguationData":[TD([[makeQuery(id+"F0.imprint","IMPRINT",EDGE,{"derivedFrom":subQ2}),-1.0]])]});}
            var Q24;
            {var subQ7=sQuery(id+"F0.wireOp",EDGE,"E49.bottom");Q24=makeQuery(id+"F0.imprint","IMPRINT",FACE,{"disambiguationData":[TD([[makeQuery(id+"F0.imprint","IMPRINT",EDGE,{"derivedFrom":subQ7}),-1.0]])]});}
            var Q25;
            {var subQ9=sQuery(id+"F0.wireOp",EDGE,"E50.bottom");Q25=makeQuery(id+"F0.imprint","IMPRINT",FACE,{"disambiguationData":[TD([[makeQuery(id+"F0.imprint","IMPRINT",EDGE,{"derivedFrom":subQ9}),-1.0]])]});}
            var Q26;
            {var subQ0=sQuery(id+"F0.wireOp",EDGE,"E69.right");Q26=makeQuery(id+"F0.imprint","IMPRINT",FACE,{"disambiguationData":[TD([[makeQuery(id+"F0.imprint","IMPRINT",EDGE,{"derivedFrom":subQ0}),-1.0]])]});}
            var Q27;
            {var subQ0=sQuery(id+"F0.wireOp",EDGE,"E71.left");Q27=makeQuery(id+"F0.imprint","IMPRINT",FACE,{"disambiguationData":[TD([[makeQuery(id+"F0.imprint","IMPRINT",EDGE,{"derivedFrom":subQ0}),1.0]])]});}
            var Q28;
            {var subQ3=sQuery(id+"F0.wireOp",EDGE,"E88.left");Q28=makeQuery(id+"F0.imprint","IMPRINT",FACE,{"disambiguationData":[TD([[makeQuery(id+"F0.imprint","IMPRINT",EDGE,{"derivedFrom":subQ3}),1.0]])]});}
            var Q29;
            {var subQ0=sQuery(id+"F0.wireOp",EDGE,"E70.right");Q29=makeQuery(id+"F0.imprint","IMPRINT",FACE,{"disambiguationData":[TD([[makeQuery(id+"F0.imprint","IMPRINT",EDGE,{"derivedFrom":subQ0}),-1.0]])]});}
            var Q30;
            {var subQ3=sQuery(id+"F0.wireOp",EDGE,"E89.left");Q30=makeQuery(id+"F0.imprint","IMPRINT",FACE,{"disambiguationData":[TD([[makeQuery(id+"F0.imprint","IMPRINT",EDGE,{"derivedFrom":subQ3}),1.0]])]});}
            var Q31;
            {var subQ3=sQuery(id+"F0.wireOp",EDGE,"E71.right");Q31=makeQuery(id+"F0.imprint","IMPRINT",FACE,{"disambiguationData":[TD([[makeQuery(id+"F0.imprint","IMPRINT",EDGE,{"derivedFrom":subQ3}),-1.0]])]});}
            var Q32;
            {var subQ0=sQuery(id+"F0.wireOp",EDGE,"E87.left");Q32=makeQuery(id+"F0.imprint","IMPRINT",FACE,{"disambiguationData":[TD([[makeQuery(id+"F0.imprint","IMPRINT",EDGE,{"derivedFrom":subQ0}),1.0]])]});}
            var Q33;
            {var subQ2=sQuery(id+"F0.wireOp",EDGE,"E0.right");Q33=makeQuery(id+"F0.imprint","IMPRINT",FACE,{"disambiguationData":[TD([[makeQuery(id+"F0.imprint","IMPRINT",EDGE,{"derivedFrom":subQ2}),1.0]])]});}
            var Q34;
            {var subQ3=sQuery(id+"F0.wireOp",EDGE,"E70.left");Q34=makeQuery(id+"F0.imprint","IMPRINT",FACE,{"disambiguationData":[TD([[makeQuery(id+"F0.imprint","IMPRINT",EDGE,{"derivedFrom":subQ3}),1.0]])]});}
            var Q35;
            {var subQ0=sQuery(id+"F0.wireOp",EDGE,"E87.right");Q35=makeQuery(id+"F0.imprint","IMPRINT",FACE,{"disambiguationData":[TD([[makeQuery(id+"F0.imprint","IMPRINT",EDGE,{"derivedFrom":subQ0}),-1.0]])]});}
            var Q36;
            {var subQ3=sQuery(id+"F0.wireOp",EDGE,"E69.left");Q36=makeQuery(id+"F0.imprint","IMPRINT",FACE,{"disambiguationData":[TD([[makeQuery(id+"F0.imprint","IMPRINT",EDGE,{"derivedFrom":subQ3}),1.0]])]});}
            var Q37;
            {var subQ0=sQuery(id+"F0.wireOp",EDGE,"E89.right");Q37=makeQuery(id+"F0.imprint","IMPRINT",FACE,{"disambiguationData":[TD([[makeQuery(id+"F0.imprint","IMPRINT",EDGE,{"derivedFrom":subQ0}),-1.0]])]});}
            var Q38;
            {var subQ0=sQuery(id+"F0.wireOp",EDGE,"E88.right");Q38=makeQuery(id+"F0.imprint","IMPRINT",FACE,{"disambiguationData":[TD([[makeQuery(id+"F0.imprint","IMPRINT",EDGE,{"derivedFrom":subQ0}),-1.0]])]});}
            var Q39;
            Q39=makeQuery(id+"F0.imprint","IMPRINT",FACE,{"disambiguationData":[TD([[makeQuery(id+"F0.imprint","IMPRINT",EDGE,{"derivedFrom":sQuery(id+"F0.wireOp",EDGE,"E101.bottom")}),-1.0]])]});
            var Q40;
            Q40=makeQuery(id+"F0.imprint","IMPRINT",FACE,{"disambiguationData":[TD([[makeQuery(id+"F0.imprint","IMPRINT",EDGE,{"derivedFrom":sQuery(id+"F0.wireOp",EDGE,"E103.bottom")}),-1.0]])]});
            var Q41;
            Q41=makeQuery(id+"F0.imprint","IMPRINT",FACE,{"disambiguationData":[TD([[makeQuery(id+"F0.imprint","IMPRINT",EDGE,{"derivedFrom":sQuery(id+"F0.wireOp",EDGE,"E37.bottom")}),-1.0]])]});
            var Q42;
            Q42=makeQuery(id+"F0.imprint","IMPRINT",FACE,{"disambiguationData":[TD([[makeQuery(id+"F0.imprint","IMPRINT",EDGE,{"derivedFrom":sQuery(id+"F0.wireOp",EDGE,"E116.bottom")}),-1.0]])]});
            var Q43;
            {var subQ2=sQuery(id+"F0.wireOp",EDGE,"E158.bottom");Q43=makeQuery(id+"F0.imprint","IMPRINT",FACE,{"disambiguationData":[TD([[makeQuery(id+"F0.imprint","IMPRINT",EDGE,{"derivedFrom":subQ2}),1.0]])]});}
            var Q44;
            {var subQ0=sQuery(id+"F0.wireOp",EDGE,"E168");Q44=makeQuery(id+"F0.imprint","IMPRINT",FACE,{"disambiguationData":[TD([[makeQuery(id+"F0.imprint","IMPRINT",EDGE,{"derivedFrom":subQ0}),-1.0]])]});}
            var Q45;
            {var subQ0=sQuery(id+"F0.wireOp",EDGE,"E172.top");var subQ3=sQuery(id+"F0.wireOp",EDGE,"E142.left");var subQ4=makeQuery(id+"F0.imprint","INTERSECT",VERTEX,{"derivedFrom":[subQ3,subQ0]});Q45=makeQuery(id+"F0.imprint","IMPRINT",FACE,{"disambiguationData":[TD([[makeQuery(id+"F0.imprint","IMPRINT",EDGE,{"disambiguationData":[TD([[subQ4,-1.0]])],"derivedFrom":subQ3}),1.0]])]});}
            var Q46;
            {var subQ0=sQuery(id+"F0.wireOp",EDGE,"E157.bottom");var subQ3=sQuery(id+"F0.wireOp",EDGE,"E140.left");var subQ4=makeQuery(id+"F0.imprint","INTERSECT",VERTEX,{"derivedFrom":[subQ3,subQ0]});Q46=makeQuery(id+"F0.imprint","IMPRINT",FACE,{"disambiguationData":[TD([[makeQuery(id+"F0.imprint","IMPRINT",EDGE,{"disambiguationData":[TD([[subQ4,1.0]])],"derivedFrom":subQ0}),1.0]])]});}
            var Q47;
            {var subQ3=sQuery(id+"F0.wireOp",EDGE,"E140.left");var subQ5=sQuery(id+"F0.wireOp",EDGE,"E157.bottom");var subQ7=makeQuery(id+"F0.imprint","INTERSECT",VERTEX,{"derivedFrom":[subQ3,subQ5]});Q47=makeQuery(id+"F0.imprint","IMPRINT",FACE,{"disambiguationData":[TD([[makeQuery(id+"F0.imprint","IMPRINT",EDGE,{"disambiguationData":[TD([[subQ7,-1.0]])],"derivedFrom":subQ3}),-1.0]])]});}
            var Q48;
            {var subQ1=sQuery(id+"F0.wireOp",EDGE,"E157.top");var subQ5=sQuery(id+"F0.wireOp",EDGE,"E140.left");var subQ6=makeQuery(id+"F0.imprint","INTERSECT",VERTEX,{"derivedFrom":[subQ5,subQ1]});Q48=makeQuery(id+"F0.imprint","IMPRINT",FACE,{"disambiguationData":[TD([[makeQuery(id+"F0.imprint","IMPRINT",EDGE,{"disambiguationData":[TD([[subQ6,1.0]])],"derivedFrom":subQ1}),-1.0]])]});}
            var Q49;
            {var subQ0=sQuery(id+"F0.wireOp",EDGE,"E157.right");Q49=makeQuery(id+"F0.imprint","IMPRINT",FACE,{"disambiguationData":[TD([[makeQuery(id+"F0.imprint","IMPRINT",EDGE,{"derivedFrom":subQ0}),-1.0]])]});}
            var Q50;
            {var subQ4=sQuery(id+"F0.wireOp",EDGE,"E139.right");Q50=makeQuery(id+"F0.imprint","IMPRINT",FACE,{"disambiguationData":[TD([[makeQuery(id+"F0.imprint","IMPRINT",EDGE,{"derivedFrom":subQ4}),1.0]])]});}
            var Q51;
            {var subQ6=sQuery(id+"F0.wireOp",EDGE,"E140.top");Q51=makeQuery(id+"F0.imprint","IMPRINT",FACE,{"disambiguationData":[TD([[makeQuery(id+"F0.imprint","IMPRINT",EDGE,{"derivedFrom":subQ6}),1.0]])]});}
            var Q52;
            {var subQ6=sQuery(id+"F0.wireOp",EDGE,"E140.bottom");Q52=makeQuery(id+"F0.imprint","IMPRINT",FACE,{"disambiguationData":[TD([[makeQuery(id+"F0.imprint","IMPRINT",EDGE,{"derivedFrom":subQ6}),-1.0]])]});}
            var Q53;
            {var subQ4=sQuery(id+"F0.wireOp",EDGE,"E139.left");Q53=makeQuery(id+"F0.imprint","IMPRINT",FACE,{"disambiguationData":[TD([[makeQuery(id+"F0.imprint","IMPRINT",EDGE,{"derivedFrom":subQ4}),-1.0]])]});}
            var Q54;
            {var subQ0=sQuery(id+"F0.wireOp",EDGE,"E157.left");Q54=makeQuery(id+"F0.imprint","IMPRINT",FACE,{"disambiguationData":[TD([[makeQuery(id+"F0.imprint","IMPRINT",EDGE,{"derivedFrom":subQ0}),1.0]])]});}
            var Q55;
            {var subQ6=sQuery(id+"F0.wireOp",EDGE,"E141.bottom");Q55=makeQuery(id+"F0.imprint","IMPRINT",FACE,{"disambiguationData":[TD([[makeQuery(id+"F0.imprint","IMPRINT",EDGE,{"derivedFrom":subQ6}),-1.0]])]});}
            var Q56;
            {var subQ4=sQuery(id+"F0.wireOp",EDGE,"E141.top");Q56=makeQuery(id+"F0.imprint","IMPRINT",FACE,{"disambiguationData":[TD([[makeQuery(id+"F0.imprint","IMPRINT",EDGE,{"derivedFrom":subQ4}),1.0]])]});}
            var Q57;
            {var subQ0=sQuery(id+"F0.wireOp",EDGE,"E171.top");var subQ3=sQuery(id+"F0.wireOp",EDGE,"E142.left");var subQ4=makeQuery(id+"F0.imprint","INTERSECT",VERTEX,{"derivedFrom":[subQ3,subQ0]});Q57=makeQuery(id+"F0.imprint","IMPRINT",FACE,{"disambiguationData":[TD([[makeQuery(id+"F0.imprint","IMPRINT",EDGE,{"disambiguationData":[TD([[subQ4,-1.0]])],"derivedFrom":subQ3}),1.0]])]});}
            var Q58;
            {var subQ0=sQuery(id+"F0.wireOp",EDGE,"E171.bottom");var subQ3=sQuery(id+"F0.wireOp",EDGE,"E142.left");var subQ4=makeQuery(id+"F0.imprint","INTERSECT",VERTEX,{"derivedFrom":[subQ3,subQ0]});Q58=makeQuery(id+"F0.imprint","IMPRINT",FACE,{"disambiguationData":[TD([[makeQuery(id+"F0.imprint","IMPRINT",EDGE,{"disambiguationData":[TD([[subQ4,1.0]])],"derivedFrom":subQ0}),1.0]])]});}
            var Q59;
            {var subQ4=sQuery(id+"F0.wireOp",EDGE,"E143.top");Q59=makeQuery(id+"F0.imprint","IMPRINT",FACE,{"disambiguationData":[TD([[makeQuery(id+"F0.imprint","IMPRINT",EDGE,{"derivedFrom":subQ4}),-1.0]])]});}
            var Q60;
            {var subQ4=sQuery(id+"F0.wireOp",EDGE,"E171.left");Q60=makeQuery(id+"F0.imprint","IMPRINT",FACE,{"disambiguationData":[TD([[makeQuery(id+"F0.imprint","IMPRINT",EDGE,{"derivedFrom":subQ4}),1.0]])]});}
            var Q61;
            {var subQ0=sQuery(id+"F0.wireOp",EDGE,"E172.top");var subQ1=sQuery(id+"F0.wireOp",EDGE,"E143.right");var subQ2=makeQuery(id+"F0.imprint","INTERSECT",VERTEX,{"derivedFrom":[subQ1,subQ0]});Q61=makeQuery(id+"F0.imprint","IMPRINT",FACE,{"disambiguationData":[TD([[makeQuery(id+"F0.imprint","IMPRINT",EDGE,{"disambiguationData":[TD([[subQ2,-1.0]])],"derivedFrom":subQ1}),1.0]])]});}
            var Q62;
            {var subQ5=sQuery(id+"F0.wireOp",EDGE,"E126.left");Q62=makeQuery(id+"F0.imprint","IMPRINT",FACE,{"disambiguationData":[TD([[makeQuery(id+"F0.imprint","IMPRINT",EDGE,{"derivedFrom":subQ5}),1.0]])]});}
            var Q63;
            {var subQ5=sQuery(id+"F0.wireOp",EDGE,"E126.right");Q63=makeQuery(id+"F0.imprint","IMPRINT",FACE,{"disambiguationData":[TD([[makeQuery(id+"F0.imprint","IMPRINT",EDGE,{"derivedFrom":subQ5}),-1.0]])]});}
            var Q64;
            {var subQ4=sQuery(id+"F0.wireOp",EDGE,"E142.top");Q64=makeQuery(id+"F0.imprint","IMPRINT",FACE,{"disambiguationData":[TD([[makeQuery(id+"F0.imprint","IMPRINT",EDGE,{"derivedFrom":subQ4}),-1.0]])]});}
            var Q65;
            {var subQ0=sQuery(id+"F0.wireOp",EDGE,"E171.right");Q65=makeQuery(id+"F0.imprint","IMPRINT",FACE,{"disambiguationData":[TD([[makeQuery(id+"F0.imprint","IMPRINT",EDGE,{"derivedFrom":subQ0}),-1.0]])]});}
            var Q66;
            {var subQ0=sQuery(id+"F0.wireOp",EDGE,"E172.top");var subQ1=sQuery(id+"F0.wireOp",EDGE,"E142.left");var subQ2=makeQuery(id+"F0.imprint","INTERSECT",VERTEX,{"derivedFrom":[subQ1,subQ0]});Q66=makeQuery(id+"F0.imprint","IMPRINT",FACE,{"disambiguationData":[TD([[makeQuery(id+"F0.imprint","IMPRINT",EDGE,{"disambiguationData":[TD([[subQ2,-1.0]])],"derivedFrom":subQ1}),-1.0]])]});}
            var Q67;
            {var subQ1=sQuery(id+"F0.wireOp",EDGE,"E172.bottom");var subQ5=sQuery(id+"F0.wireOp",EDGE,"E142.left");var subQ6=makeQuery(id+"F0.imprint","INTERSECT",VERTEX,{"derivedFrom":[subQ5,subQ1]});Q67=makeQuery(id+"F0.imprint","IMPRINT",FACE,{"disambiguationData":[TD([[makeQuery(id+"F0.imprint","IMPRINT",EDGE,{"disambiguationData":[TD([[subQ6,1.0]])],"derivedFrom":subQ1}),-1.0]])]});}
            var Q68;
            {var subQ3=sQuery(id+"F0.wireOp",EDGE,"E142.left");var subQ5=sQuery(id+"F0.wireOp",EDGE,"E172.bottom");var subQ7=makeQuery(id+"F0.imprint","INTERSECT",VERTEX,{"derivedFrom":[subQ3,subQ5]});Q68=makeQuery(id+"F0.imprint","IMPRINT",FACE,{"disambiguationData":[TD([[makeQuery(id+"F0.imprint","IMPRINT",EDGE,{"disambiguationData":[TD([[subQ7,-1.0]])],"derivedFrom":subQ3}),1.0]])]});}
            var Q69;
            {var subQ0=sQuery(id+"F0.wireOp",EDGE,"E172.right");Q69=makeQuery(id+"F0.imprint","IMPRINT",FACE,{"disambiguationData":[TD([[makeQuery(id+"F0.imprint","IMPRINT",EDGE,{"derivedFrom":subQ0}),1.0]])]});}
            var Q70;
            {var subQ6=sQuery(id+"F0.wireOp",EDGE,"E142.bottom");Q70=makeQuery(id+"F0.imprint","IMPRINT",FACE,{"disambiguationData":[TD([[makeQuery(id+"F0.imprint","IMPRINT",EDGE,{"derivedFrom":subQ6}),1.0]])]});}
            var Q71;
            {var subQ0=sQuery(id+"F0.wireOp",EDGE,"E172.left");Q71=makeQuery(id+"F0.imprint","IMPRINT",FACE,{"disambiguationData":[TD([[makeQuery(id+"F0.imprint","IMPRINT",EDGE,{"derivedFrom":subQ0}),-1.0]])]});}
            var Q72;
            {var subQ4=sQuery(id+"F0.wireOp",EDGE,"E143.bottom");Q72=makeQuery(id+"F0.imprint","IMPRINT",FACE,{"disambiguationData":[TD([[makeQuery(id+"F0.imprint","IMPRINT",EDGE,{"derivedFrom":subQ4}),1.0]])]});}
            var Q73;
            {var subQ17=sQuery(id+"F0.wireOp",EDGE,"E26.top");Q73=makeQuery(id+"F0.imprint","IMPRINT",FACE,{"disambiguationData":[TD([[makeQuery(id+"F0.imprint","IMPRINT",EDGE,{"derivedFrom":subQ17}),1.0]])]});}
            var Q74;
            {var subQ16=sQuery(id+"F0.wireOp",EDGE,"E27.top");Q74=makeQuery(id+"F0.imprint","IMPRINT",FACE,{"disambiguationData":[TD([[makeQuery(id+"F0.imprint","IMPRINT",EDGE,{"derivedFrom":subQ16}),1.0]])]});}
            var Q75;
            {var subQ1=sQuery(id+"F0.wireOp",EDGE,"E165");Q75=makeQuery(id+"F0.imprint","IMPRINT",FACE,{"disambiguationData":[TD([[makeQuery(id+"F0.imprint","IMPRINT",EDGE,{"derivedFrom":subQ1}),-1.0]])]});}
            var Q76;
            {var subQ2=sQuery(id+"F0.wireOp",EDGE,"E135");Q76=makeQuery(id+"F0.imprint","IMPRINT",FACE,{"disambiguationData":[TD([[makeQuery(id+"F0.imprint","IMPRINT",EDGE,{"derivedFrom":subQ2}),-1.0]])]});}
            var Q77;
            {var subQ2=sQuery(id+"F0.wireOp",EDGE,"E131");Q77=makeQuery(id+"F0.imprint","IMPRINT",FACE,{"disambiguationData":[TD([[makeQuery(id+"F0.imprint","IMPRINT",EDGE,{"derivedFrom":subQ2}),1.0]])]});}
            var Q78;
            {var subQ1=sQuery(id+"F0.wireOp",EDGE,"E167");Q78=makeQuery(id+"F0.imprint","IMPRINT",FACE,{"disambiguationData":[TD([[makeQuery(id+"F0.imprint","IMPRINT",EDGE,{"derivedFrom":subQ1}),-1.0]])]});}
            var Q79;
            {var subQ0=sQuery(id+"F0.wireOp",EDGE,"E138");Q79=makeQuery(id+"F0.imprint","IMPRINT",FACE,{"disambiguationData":[TD([[makeQuery(id+"F0.imprint","IMPRINT",EDGE,{"derivedFrom":subQ0}),-1.0]])]});}
            var Q80;
            {var subQ0=sQuery(id+"F0.wireOp",EDGE,"E159.right");Q80=makeQuery(id+"F0.imprint","IMPRINT",FACE,{"disambiguationData":[TD([[makeQuery(id+"F0.imprint","IMPRINT",EDGE,{"derivedFrom":subQ0}),-1.0]])]});}
            var Q81;
            {var subQ2=sQuery(id+"F0.wireOp",EDGE,"E129");Q81=makeQuery(id+"F0.imprint","IMPRINT",FACE,{"disambiguationData":[TD([[makeQuery(id+"F0.imprint","IMPRINT",EDGE,{"derivedFrom":subQ2}),1.0]])]});}
            var Q82;
            Q82=makeQuery(id+"F0.imprint","IMPRINT",FACE,{"disambiguationData":[TD([[makeQuery(id+"F0.imprint","IMPRINT",EDGE,{"derivedFrom":sQuery(id+"F0.wireOp",EDGE,"E158.bottom")}),-1.0]])]});
            var Q83;
            {var subQ0=sQuery(id+"F0.wireOp",EDGE,"E159.left");Q83=makeQuery(id+"F0.imprint","IMPRINT",FACE,{"disambiguationData":[TD([[makeQuery(id+"F0.imprint","IMPRINT",EDGE,{"derivedFrom":subQ0}),1.0]])]});}
            extrude(context, id + "F1", {"entities" : qUnion([Q0, Q1, Q2, Q3, Q4, Q5, Q6, Q7, Q8, Q9, Q10, Q11, Q12, Q13, Q14, Q15, Q16, Q17, Q18, Q19, Q20, Q21, Q22, Q23, Q24, Q25, Q26, Q27, Q28, Q29, Q30, Q31, Q32, Q33, Q34, Q35, Q36, Q37, Q38, Q39, Q40, Q41, Q42, Q43, Q44, Q45, Q46, Q47, Q48, Q49, Q50, Q51, Q52, Q53, Q54, Q55, Q56, Q57, Q58, Q59, Q60, Q61, Q62, Q63, Q64, Q65, Q66, Q67, Q68, Q69, Q70, Q71, Q72, Q73, Q74, Q75, Q76, Q77, Q78, Q79, Q80, Q81, Q82, Q83]), "oppositeDirection" : true, "depth" : 12 * mm});
        }
        {
            var Q0;
            {var subQ3=sQuery(id+"F0.wireOp",EDGE,"E49.right");var subQ5=sQuery(id+"F0.wireOp",EDGE,"E71.bottom");var subQ7=makeQuery(id+"F0.imprint","INTERSECT",VERTEX,{"derivedFrom":[subQ3,subQ5]});Q0=makeQuery(id+"F0.imprint","IMPRINT",FACE,{"disambiguationData":[TD([[makeQuery(id+"F0.imprint","IMPRINT",EDGE,{"disambiguationData":[TD([[subQ7,-1.0]])],"derivedFrom":subQ3}),1.0]])]});}
            var Q1;
            {var subQ3=sQuery(id+"F0.wireOp",EDGE,"E49.right");var subQ5=sQuery(id+"F0.wireOp",EDGE,"E70.bottom");var subQ7=makeQuery(id+"F0.imprint","INTERSECT",VERTEX,{"derivedFrom":[subQ3,subQ5]});Q1=makeQuery(id+"F0.imprint","IMPRINT",FACE,{"disambiguationData":[TD([[makeQuery(id+"F0.imprint","IMPRINT",EDGE,{"disambiguationData":[TD([[subQ7,-1.0]])],"derivedFrom":subQ3}),1.0]])]});}
            var Q2;
            {var subQ0=sQuery(id+"F0.wireOp",EDGE,"E69.bottom");var subQ3=sQuery(id+"F0.wireOp",EDGE,"E49.right");var subQ4=makeQuery(id+"F0.imprint","INTERSECT",VERTEX,{"derivedFrom":[subQ3,subQ0]});Q2=makeQuery(id+"F0.imprint","IMPRINT",FACE,{"disambiguationData":[TD([[makeQuery(id+"F0.imprint","IMPRINT",EDGE,{"disambiguationData":[TD([[subQ4,-1.0]])],"derivedFrom":subQ3}),1.0]])]});}
            var Q3;
            {var subQ7=sQuery(id+"F0.wireOp",EDGE,"E49.bottom");Q3=makeQuery(id+"F0.imprint","IMPRINT",FACE,{"disambiguationData":[TD([[makeQuery(id+"F0.imprint","IMPRINT",EDGE,{"derivedFrom":subQ7}),-1.0]])]});}
            var Q4;
            {var subQ3=sQuery(id+"F0.wireOp",EDGE,"E69.left");Q4=makeQuery(id+"F0.imprint","IMPRINT",FACE,{"disambiguationData":[TD([[makeQuery(id+"F0.imprint","IMPRINT",EDGE,{"derivedFrom":subQ3}),1.0]])]});}
            var Q5;
            {var subQ0=sQuery(id+"F0.wireOp",EDGE,"E71.left");Q5=makeQuery(id+"F0.imprint","IMPRINT",FACE,{"disambiguationData":[TD([[makeQuery(id+"F0.imprint","IMPRINT",EDGE,{"derivedFrom":subQ0}),1.0]])]});}
            var Q6;
            {var subQ3=sQuery(id+"F0.wireOp",EDGE,"E70.left");Q6=makeQuery(id+"F0.imprint","IMPRINT",FACE,{"disambiguationData":[TD([[makeQuery(id+"F0.imprint","IMPRINT",EDGE,{"derivedFrom":subQ3}),1.0]])]});}
            var Q7;
            {var subQ0=sQuery(id+"F0.wireOp",EDGE,"E70.right");Q7=makeQuery(id+"F0.imprint","IMPRINT",FACE,{"disambiguationData":[TD([[makeQuery(id+"F0.imprint","IMPRINT",EDGE,{"derivedFrom":subQ0}),-1.0]])]});}
            var Q8;
            {var subQ3=sQuery(id+"F0.wireOp",EDGE,"E71.right");Q8=makeQuery(id+"F0.imprint","IMPRINT",FACE,{"disambiguationData":[TD([[makeQuery(id+"F0.imprint","IMPRINT",EDGE,{"derivedFrom":subQ3}),-1.0]])]});}
            var Q9;
            {var subQ9=sQuery(id+"F0.wireOp",EDGE,"E50.bottom");Q9=makeQuery(id+"F0.imprint","IMPRINT",FACE,{"disambiguationData":[TD([[makeQuery(id+"F0.imprint","IMPRINT",EDGE,{"derivedFrom":subQ9}),-1.0]])]});}
            var Q10;
            {var subQ0=sQuery(id+"F0.wireOp",EDGE,"E69.right");Q10=makeQuery(id+"F0.imprint","IMPRINT",FACE,{"disambiguationData":[TD([[makeQuery(id+"F0.imprint","IMPRINT",EDGE,{"derivedFrom":subQ0}),-1.0]])]});}
            var Q11;
            {var subQ3=sQuery(id+"F0.wireOp",EDGE,"E140.left");var subQ5=sQuery(id+"F0.wireOp",EDGE,"E157.bottom");var subQ7=makeQuery(id+"F0.imprint","INTERSECT",VERTEX,{"derivedFrom":[subQ3,subQ5]});Q11=makeQuery(id+"F0.imprint","IMPRINT",FACE,{"disambiguationData":[TD([[makeQuery(id+"F0.imprint","IMPRINT",EDGE,{"disambiguationData":[TD([[subQ7,-1.0]])],"derivedFrom":subQ3}),-1.0]])]});}
            var Q12;
            {var subQ0=sQuery(id+"F0.wireOp",EDGE,"E157.left");Q12=makeQuery(id+"F0.imprint","IMPRINT",FACE,{"disambiguationData":[TD([[makeQuery(id+"F0.imprint","IMPRINT",EDGE,{"derivedFrom":subQ0}),1.0]])]});}
            var Q13;
            {var subQ6=sQuery(id+"F0.wireOp",EDGE,"E141.bottom");Q13=makeQuery(id+"F0.imprint","IMPRINT",FACE,{"disambiguationData":[TD([[makeQuery(id+"F0.imprint","IMPRINT",EDGE,{"derivedFrom":subQ6}),-1.0]])]});}
            var Q14;
            {var subQ4=sQuery(id+"F0.wireOp",EDGE,"E141.top");Q14=makeQuery(id+"F0.imprint","IMPRINT",FACE,{"disambiguationData":[TD([[makeQuery(id+"F0.imprint","IMPRINT",EDGE,{"derivedFrom":subQ4}),1.0]])]});}
            var Q15;
            {var subQ6=sQuery(id+"F0.wireOp",EDGE,"E140.bottom");Q15=makeQuery(id+"F0.imprint","IMPRINT",FACE,{"disambiguationData":[TD([[makeQuery(id+"F0.imprint","IMPRINT",EDGE,{"derivedFrom":subQ6}),-1.0]])]});}
            var Q16;
            {var subQ0=sQuery(id+"F0.wireOp",EDGE,"E157.right");Q16=makeQuery(id+"F0.imprint","IMPRINT",FACE,{"disambiguationData":[TD([[makeQuery(id+"F0.imprint","IMPRINT",EDGE,{"derivedFrom":subQ0}),-1.0]])]});}
            var Q17;
            {var subQ6=sQuery(id+"F0.wireOp",EDGE,"E140.top");Q17=makeQuery(id+"F0.imprint","IMPRINT",FACE,{"disambiguationData":[TD([[makeQuery(id+"F0.imprint","IMPRINT",EDGE,{"derivedFrom":subQ6}),1.0]])]});}
            var Q18;
            {var subQ0=sQuery(id+"F0.wireOp",EDGE,"E171.top");var subQ3=sQuery(id+"F0.wireOp",EDGE,"E142.left");var subQ4=makeQuery(id+"F0.imprint","INTERSECT",VERTEX,{"derivedFrom":[subQ3,subQ0]});Q18=makeQuery(id+"F0.imprint","IMPRINT",FACE,{"disambiguationData":[TD([[makeQuery(id+"F0.imprint","IMPRINT",EDGE,{"disambiguationData":[TD([[subQ4,-1.0]])],"derivedFrom":subQ3}),1.0]])]});}
            var Q19;
            {var subQ3=sQuery(id+"F0.wireOp",EDGE,"E142.left");var subQ5=sQuery(id+"F0.wireOp",EDGE,"E172.bottom");var subQ7=makeQuery(id+"F0.imprint","INTERSECT",VERTEX,{"derivedFrom":[subQ3,subQ5]});Q19=makeQuery(id+"F0.imprint","IMPRINT",FACE,{"disambiguationData":[TD([[makeQuery(id+"F0.imprint","IMPRINT",EDGE,{"disambiguationData":[TD([[subQ7,-1.0]])],"derivedFrom":subQ3}),1.0]])]});}
            var Q20;
            {var subQ0=sQuery(id+"F0.wireOp",EDGE,"E172.top");var subQ1=sQuery(id+"F0.wireOp",EDGE,"E143.right");var subQ2=makeQuery(id+"F0.imprint","INTERSECT",VERTEX,{"derivedFrom":[subQ1,subQ0]});Q20=makeQuery(id+"F0.imprint","IMPRINT",FACE,{"disambiguationData":[TD([[makeQuery(id+"F0.imprint","IMPRINT",EDGE,{"disambiguationData":[TD([[subQ2,-1.0]])],"derivedFrom":subQ1}),1.0]])]});}
            var Q21;
            {var subQ0=sQuery(id+"F0.wireOp",EDGE,"E172.top");var subQ1=sQuery(id+"F0.wireOp",EDGE,"E142.left");var subQ2=makeQuery(id+"F0.imprint","INTERSECT",VERTEX,{"derivedFrom":[subQ1,subQ0]});Q21=makeQuery(id+"F0.imprint","IMPRINT",FACE,{"disambiguationData":[TD([[makeQuery(id+"F0.imprint","IMPRINT",EDGE,{"disambiguationData":[TD([[subQ2,-1.0]])],"derivedFrom":subQ1}),-1.0]])]});}
            var Q22;
            {var subQ4=sQuery(id+"F0.wireOp",EDGE,"E142.top");Q22=makeQuery(id+"F0.imprint","IMPRINT",FACE,{"disambiguationData":[TD([[makeQuery(id+"F0.imprint","IMPRINT",EDGE,{"derivedFrom":subQ4}),-1.0]])]});}
            var Q23;
            {var subQ0=sQuery(id+"F0.wireOp",EDGE,"E171.right");Q23=makeQuery(id+"F0.imprint","IMPRINT",FACE,{"disambiguationData":[TD([[makeQuery(id+"F0.imprint","IMPRINT",EDGE,{"derivedFrom":subQ0}),-1.0]])]});}
            var Q24;
            {var subQ0=sQuery(id+"F0.wireOp",EDGE,"E172.right");Q24=makeQuery(id+"F0.imprint","IMPRINT",FACE,{"disambiguationData":[TD([[makeQuery(id+"F0.imprint","IMPRINT",EDGE,{"derivedFrom":subQ0}),1.0]])]});}
            var Q25;
            {var subQ6=sQuery(id+"F0.wireOp",EDGE,"E142.bottom");Q25=makeQuery(id+"F0.imprint","IMPRINT",FACE,{"disambiguationData":[TD([[makeQuery(id+"F0.imprint","IMPRINT",EDGE,{"derivedFrom":subQ6}),1.0]])]});}
            var Q26;
            {var subQ4=sQuery(id+"F0.wireOp",EDGE,"E143.bottom");Q26=makeQuery(id+"F0.imprint","IMPRINT",FACE,{"disambiguationData":[TD([[makeQuery(id+"F0.imprint","IMPRINT",EDGE,{"derivedFrom":subQ4}),1.0]])]});}
            var Q27;
            {var subQ0=sQuery(id+"F0.wireOp",EDGE,"E172.left");Q27=makeQuery(id+"F0.imprint","IMPRINT",FACE,{"disambiguationData":[TD([[makeQuery(id+"F0.imprint","IMPRINT",EDGE,{"derivedFrom":subQ0}),-1.0]])]});}
            var Q28;
            {var subQ4=sQuery(id+"F0.wireOp",EDGE,"E171.left");Q28=makeQuery(id+"F0.imprint","IMPRINT",FACE,{"disambiguationData":[TD([[makeQuery(id+"F0.imprint","IMPRINT",EDGE,{"derivedFrom":subQ4}),1.0]])]});}
            var Q29;
            {var subQ4=sQuery(id+"F0.wireOp",EDGE,"E143.top");Q29=makeQuery(id+"F0.imprint","IMPRINT",FACE,{"disambiguationData":[TD([[makeQuery(id+"F0.imprint","IMPRINT",EDGE,{"derivedFrom":subQ4}),-1.0]])]});}
            var Q30;
            {var subQ0=sQuery(id+"F0.wireOp",EDGE,"E87.bottom");var subQ3=sQuery(id+"F0.wireOp",EDGE,"E26.right");var subQ4=makeQuery(id+"F0.imprint","INTERSECT",VERTEX,{"derivedFrom":[subQ3,subQ0]});Q30=makeQuery(id+"F0.imprint","IMPRINT",FACE,{"disambiguationData":[TD([[makeQuery(id+"F0.imprint","IMPRINT",EDGE,{"disambiguationData":[TD([[subQ4,-1.0]])],"derivedFrom":subQ3}),1.0]])]});}
            var Q31;
            {var subQ3=sQuery(id+"F0.wireOp",EDGE,"E26.right");var subQ5=sQuery(id+"F0.wireOp",EDGE,"E88.bottom");var subQ7=makeQuery(id+"F0.imprint","INTERSECT",VERTEX,{"derivedFrom":[subQ3,subQ5]});Q31=makeQuery(id+"F0.imprint","IMPRINT",FACE,{"disambiguationData":[TD([[makeQuery(id+"F0.imprint","IMPRINT",EDGE,{"disambiguationData":[TD([[subQ7,-1.0]])],"derivedFrom":subQ3}),1.0]])]});}
            var Q32;
            {var subQ0=sQuery(id+"F0.wireOp",EDGE,"E89.bottom");var subQ3=sQuery(id+"F0.wireOp",EDGE,"E26.right");var subQ4=makeQuery(id+"F0.imprint","INTERSECT",VERTEX,{"derivedFrom":[subQ3,subQ0]});Q32=makeQuery(id+"F0.imprint","IMPRINT",FACE,{"disambiguationData":[TD([[makeQuery(id+"F0.imprint","IMPRINT",EDGE,{"disambiguationData":[TD([[subQ4,-1.0]])],"derivedFrom":subQ3}),1.0]])]});}
            var Q33;
            {var subQ17=sQuery(id+"F0.wireOp",EDGE,"E26.top");Q33=makeQuery(id+"F0.imprint","IMPRINT",FACE,{"disambiguationData":[TD([[makeQuery(id+"F0.imprint","IMPRINT",EDGE,{"derivedFrom":subQ17}),1.0]])]});}
            var Q34;
            {var subQ16=sQuery(id+"F0.wireOp",EDGE,"E27.top");Q34=makeQuery(id+"F0.imprint","IMPRINT",FACE,{"disambiguationData":[TD([[makeQuery(id+"F0.imprint","IMPRINT",EDGE,{"derivedFrom":subQ16}),1.0]])]});}
            var Q35;
            {var subQ0=sQuery(id+"F0.wireOp",EDGE,"E87.left");Q35=makeQuery(id+"F0.imprint","IMPRINT",FACE,{"disambiguationData":[TD([[makeQuery(id+"F0.imprint","IMPRINT",EDGE,{"derivedFrom":subQ0}),1.0]])]});}
            var Q36;
            {var subQ3=sQuery(id+"F0.wireOp",EDGE,"E88.left");Q36=makeQuery(id+"F0.imprint","IMPRINT",FACE,{"disambiguationData":[TD([[makeQuery(id+"F0.imprint","IMPRINT",EDGE,{"derivedFrom":subQ3}),1.0]])]});}
            var Q37;
            {var subQ3=sQuery(id+"F0.wireOp",EDGE,"E89.left");Q37=makeQuery(id+"F0.imprint","IMPRINT",FACE,{"disambiguationData":[TD([[makeQuery(id+"F0.imprint","IMPRINT",EDGE,{"derivedFrom":subQ3}),1.0]])]});}
            var Q38;
            {var subQ0=sQuery(id+"F0.wireOp",EDGE,"E87.right");Q38=makeQuery(id+"F0.imprint","IMPRINT",FACE,{"disambiguationData":[TD([[makeQuery(id+"F0.imprint","IMPRINT",EDGE,{"derivedFrom":subQ0}),-1.0]])]});}
            var Q39;
            {var subQ0=sQuery(id+"F0.wireOp",EDGE,"E88.right");Q39=makeQuery(id+"F0.imprint","IMPRINT",FACE,{"disambiguationData":[TD([[makeQuery(id+"F0.imprint","IMPRINT",EDGE,{"derivedFrom":subQ0}),-1.0]])]});}
            var Q40;
            {var subQ0=sQuery(id+"F0.wireOp",EDGE,"E89.right");Q40=makeQuery(id+"F0.imprint","IMPRINT",FACE,{"disambiguationData":[TD([[makeQuery(id+"F0.imprint","IMPRINT",EDGE,{"derivedFrom":subQ0}),-1.0]])]});}
            var Q41;
            {var subQ1=sQuery(id+"F0.wireOp",EDGE,"E165");Q41=makeQuery(id+"F0.imprint","IMPRINT",FACE,{"disambiguationData":[TD([[makeQuery(id+"F0.imprint","IMPRINT",EDGE,{"derivedFrom":subQ1}),-1.0]])]});}
            var Q42;
            {var subQ1=sQuery(id+"F0.wireOp",EDGE,"E167");Q42=makeQuery(id+"F0.imprint","IMPRINT",FACE,{"disambiguationData":[TD([[makeQuery(id+"F0.imprint","IMPRINT",EDGE,{"derivedFrom":subQ1}),-1.0]])]});}
            var Q43;
            {var subQ0=sQuery(id+"F0.wireOp",EDGE,"E159.right");Q43=makeQuery(id+"F0.imprint","IMPRINT",FACE,{"disambiguationData":[TD([[makeQuery(id+"F0.imprint","IMPRINT",EDGE,{"derivedFrom":subQ0}),-1.0]])]});}
            var Q44;
            Q44=makeQuery(id+"F0.imprint","IMPRINT",FACE,{"disambiguationData":[TD([[makeQuery(id+"F0.imprint","IMPRINT",EDGE,{"derivedFrom":sQuery(id+"F0.wireOp",EDGE,"E158.bottom")}),-1.0]])]});
            var Q45;
            {var subQ1=sQuery(id+"F0.wireOp",EDGE,"E97.bottom");Q45=makeQuery(id+"F0.imprint","IMPRINT",FACE,{"disambiguationData":[TD([[makeQuery(id+"F0.imprint","IMPRINT",EDGE,{"derivedFrom":subQ1}),1.0]])]});}
            var Q46;
            Q46=makeQuery(id+"F0.imprint","IMPRINT",FACE,{"disambiguationData":[TD([[makeQuery(id+"F0.imprint","IMPRINT",EDGE,{"derivedFrom":sQuery(id+"F0.wireOp",EDGE,"E99.bottom")}),1.0]])]});
            var Q47;
            {var subQ1=sQuery(id+"F0.wireOp",EDGE,"E98.bottom");Q47=makeQuery(id+"F0.imprint","IMPRINT",FACE,{"disambiguationData":[TD([[makeQuery(id+"F0.imprint","IMPRINT",EDGE,{"derivedFrom":subQ1}),1.0]])]});}
            extrude(context, id + "F2", {"entities" : qUnion([Q0, Q1, Q2, Q3, Q4, Q5, Q6, Q7, Q8, Q9, Q10, Q11, Q12, Q13, Q14, Q15, Q16, Q17, Q18, Q19, Q20, Q21, Q22, Q23, Q24, Q25, Q26, Q27, Q28, Q29, Q30, Q31, Q32, Q33, Q34, Q35, Q36, Q37, Q38, Q39, Q40, Q41, Q42, Q43, Q44, Q45, Q46, Q47]), "operationType" : NewBodyOperationType.REMOVE, "oppositeDirection" : true, "depth" : 6 * mm});
        }
        {
            var Q0;
            {var subQ3=sQuery(id+"F0.wireOp",EDGE,"E26.right");var subQ5=sQuery(id+"F0.wireOp",EDGE,"E88.top");var subQ7=makeQuery(id+"F0.imprint","INTERSECT",VERTEX,{"derivedFrom":[subQ3,subQ5]});Q0=makeQuery(id+"F0.imprint","IMPRINT",FACE,{"disambiguationData":[TD([[makeQuery(id+"F0.imprint","IMPRINT",EDGE,{"disambiguationData":[TD([[subQ7,-1.0]])],"derivedFrom":subQ3}),1.0]])]});}
            var sketch = newSketch(context, id + "F3", { "sketchPlane" : qUnion([Q0])});
            skLineSegment(sketch, "E173.0", {"start": v(-1603.84, 505) * mm, "end": v(2199.75, 505) * mm, "construction": true});
            skLineSegment(sketch, "E174.0", {"start": v(-1603.84, 0) * mm, "end": v(2199.75, 0) * mm, "construction": true});
            skLineSegment(sketch, "E175.0", {"start": v(461.84, -1362.13) * mm, "end": v(461.84, 1728.44) * mm, "construction": true});
            skLineSegment(sketch, "E176.0", {"start": v(-158.16, -1362.13) * mm, "end": v(-158.16, 1728.44) * mm, "construction": true});
            skLineSegment(sketch, "E177", {"start": v(-171.82, 505) * mm, "end": v(-171.82, 451) * mm, "construction": true});
            skLineSegment(sketch, "E178", {"start": v(-171.82, 451) * mm, "end": v(840.9, 451) * mm, "construction": true});
            skLineSegment(sketch, "E179.0", {"start": v(-158.16, 1310) * mm, "end": v(461.84, 1310) * mm, "construction": true});
            skLineSegment(sketch, "E180", {"start": v(-158.16, 1310) * mm, "end": v(-171.82, 1310) * mm, "construction": true});
            skLineSegment(sketch, "E181", {"start": v(-171.82, 1310) * mm, "end": v(-171.82, 1256) * mm, "construction": true});
            skLineSegment(sketch, "E182", {"start": v(-171.82, 1256) * mm, "end": v(-171.82, 1241) * mm, "construction": true});
            skLineSegment(sketch, "E183", {"start": v(-171.82, 1256) * mm, "end": v(461.84, 1256) * mm, "construction": true});
            skLineSegment(sketch, "E184", {"start": v(-171.82, 1241) * mm, "end": v(461.84, 1241) * mm, "construction": true});
            skLineSegment(sketch, "E185", {"start": v(-171.82, 451) * mm, "end": v(-171.82, 436) * mm, "construction": true});
            skLineSegment(sketch, "E186", {"start": v(-171.82, 436) * mm, "end": v(840.9, 436) * mm, "construction": true});
            skLineSegment(sketch, "E187", {"start": v(-96.16, 1183.53) * mm, "end": v(-96.16, 436) * mm, "construction": true});
            skLineSegment(sketch, "E188", {"start": v(461.84, 1183.53) * mm, "end": v(461.84, 1310) * mm, "construction": true});
            skLineSegment(sketch, "E189", {"start": v(399.84, 1198.1) * mm, "end": v(399.84, 436) * mm, "construction": true});
            skLineSegment(sketch, "E190.0", {"start": v(510.9, 0) * mm, "end": v(510.9, 505) * mm, "construction": true});
            skLineSegment(sketch, "E191.0", {"start": v(840.9, 505) * mm, "end": v(840.9, 0) * mm, "construction": true});
            skLineSegment(sketch, "E192", {"start": v(516.9, 424.41) * mm, "end": v(556.9, 424.41) * mm, "construction": true});
            skLineSegment(sketch, "E193", {"start": v(556.9, 436) * mm, "end": v(556.9, 424.41) * mm, "construction": true});
            skLineSegment(sketch, "E194", {"start": v(834.9, 424.41) * mm, "end": v(794.9, 424.41) * mm, "construction": true});
            skLineSegment(sketch, "E195", {"start": v(794.9, 436) * mm, "end": v(794.9, 424.41) * mm, "construction": true});
            skCircle(sketch, "E196", {"center": v(-96.16, 1256) * mm, "radius": 6 * mm, "construction": true});
            skCircle(sketch, "E197", {"center": v(-96.16, 1241) * mm, "radius": 6 * mm});
            skCircle(sketch, "E198", {"center": v(399.84, 1256) * mm, "radius": 6 * mm, "construction": true});
            skCircle(sketch, "E199", {"center": v(399.84, 1241) * mm, "radius": 6 * mm});
            skCircle(sketch, "E200", {"center": v(-96.16, 451) * mm, "radius": 6 * mm, "construction": true});
            skCircle(sketch, "E201", {"center": v(-96.16, 436) * mm, "radius": 6 * mm});
            skCircle(sketch, "E202", {"center": v(399.84, 451) * mm, "radius": 6 * mm, "construction": true});
            skCircle(sketch, "E203", {"center": v(399.84, 436) * mm, "radius": 6 * mm});
            skCircle(sketch, "E204", {"center": v(556.9, 451) * mm, "radius": 6 * mm});
            skCircle(sketch, "E205", {"center": v(556.9, 436) * mm, "radius": 6 * mm, "construction": true});
            skCircle(sketch, "E206", {"center": v(794.9, 451) * mm, "radius": 6 * mm});
            skCircle(sketch, "E207", {"center": v(794.9, 436) * mm, "radius": 6 * mm, "construction": true});
            skLineSegment(sketch, "E208", {"start": v(-158.16, -36.55) * mm, "end": v(48.5, -36.55) * mm, "construction": true});
            skLineSegment(sketch, "E209", {"start": v(48.5, -36.55) * mm, "end": v(255.17, -36.55) * mm, "construction": true});
            skLineSegment(sketch, "E210", {"start": v(255.17, -36.55) * mm, "end": v(461.84, -36.55) * mm, "construction": true});
            skLineSegment(sketch, "E211", {"start": v(48.5, -36.55) * mm, "end": v(48.5, 1728.44) * mm, "construction": true});
            skLineSegment(sketch, "E212", {"start": v(255.17, -36.55) * mm, "end": v(255.17, 1728.44) * mm, "construction": true});
            skLineSegment(sketch, "E213", {"start": v(48.5, -36.55) * mm, "end": v(48.5, -1362.13) * mm, "construction": true});
            skLineSegment(sketch, "E214", {"start": v(255.17, -36.55) * mm, "end": v(255.17, -1362.13) * mm, "construction": true});
            skLineSegment(sketch, "E215.0", {"start": v(-142.16, 495) * mm, "end": v(-142.16, 483) * mm, "construction": true});
            skLineSegment(sketch, "E216.1", {"start": v(-142.16, 413) * mm, "end": v(-142.16, 401) * mm, "construction": true});
            skLineSegment(sketch, "E217.0", {"start": v(-142.16, 122) * mm, "end": v(-142.16, 110) * mm});
            skLineSegment(sketch, "E218", {"start": v(-142.16, 489) * mm, "end": v(840.9, 489) * mm, "construction": true});
            skLineSegment(sketch, "E219", {"start": v(-142.16, 407) * mm, "end": v(840.9, 407) * mm, "construction": true});
            skLineSegment(sketch, "E220", {"start": v(-142.16, 116) * mm, "end": v(840.9, 116) * mm, "construction": true});
            skLineSegment(sketch, "E221.0", {"start": v(445.84, 1310) * mm, "end": v(445.84, -1362.13) * mm, "construction": true});
            skLineSegment(sketch, "E222.0", {"start": v(-142.16, 1310) * mm, "end": v(-142.16, -1362.13) * mm, "construction": true});
            skCircle(sketch, "E223", {"center": v(48.5, 489) * mm, "radius": 2.5 * mm});
            skCircle(sketch, "E224", {"center": v(255.17, 489) * mm, "radius": 2.5 * mm});
            skCircle(sketch, "E225", {"center": v(48.5, 407) * mm, "radius": 2.5 * mm});
            skCircle(sketch, "E226", {"center": v(255.17, 407) * mm, "radius": 2.5 * mm});
            skCircle(sketch, "E227", {"center": v(48.5, 116) * mm, "radius": 2.5 * mm});
            skCircle(sketch, "E228", {"center": v(255.17, 116) * mm, "radius": 2.5 * mm});
            skLineSegment(sketch, "E229", {"start": v(510.9, 0) * mm, "end": v(510.9, -36.55) * mm, "construction": true});
            skLineSegment(sketch, "E230", {"start": v(461.84, -36.55) * mm, "end": v(510.9, -36.55) * mm, "construction": true});
            skLineSegment(sketch, "E231", {"start": v(510.9, -36.55) * mm, "end": v(620.9, -36.55) * mm, "construction": true});
            skLineSegment(sketch, "E232", {"start": v(620.9, -36.55) * mm, "end": v(730.9, -36.55) * mm, "construction": true});
            skLineSegment(sketch, "E233", {"start": v(730.9, -36.55) * mm, "end": v(840.9, -36.55) * mm, "construction": true});
            skLineSegment(sketch, "E234", {"start": v(840.9, -36.55) * mm, "end": v(840.9, 0) * mm, "construction": true});
            skLineSegment(sketch, "E235", {"start": v(620.9, -36.55) * mm, "end": v(620.9, 489) * mm, "construction": true});
            skLineSegment(sketch, "E236", {"start": v(730.9, -36.55) * mm, "end": v(730.9, 489) * mm, "construction": true});
            skCircle(sketch, "E237", {"center": v(620.9, 489) * mm, "radius": 2.5 * mm});
            skCircle(sketch, "E238", {"center": v(730.9, 489) * mm, "radius": 2.5 * mm});
            skCircle(sketch, "E239", {"center": v(620.9, 407) * mm, "radius": 2.5 * mm});
            skCircle(sketch, "E240", {"center": v(730.9, 407) * mm, "radius": 2.5 * mm});
            skCircle(sketch, "E241", {"center": v(620.9, 116) * mm, "radius": 2.5 * mm});
            skCircle(sketch, "E242", {"center": v(730.9, 116) * mm, "radius": 2.5 * mm});
            skLineSegment(sketch, "E243.0", {"start": v(-108.16, 0) * mm, "end": v(-108.16, 100) * mm, "construction": true});
            skLineSegment(sketch, "E244", {"start": v(-108.16, 50) * mm, "end": v(-142.16, 50) * mm, "construction": true});
            skLineSegment(sketch, "E245", {"start": v(-108.16, 50) * mm, "end": v(840.9, 50) * mm, "construction": true});
            skCircle(sketch, "E246", {"center": v(-142.16, 50) * mm, "radius": 2.5 * mm});
            skCircle(sketch, "E247", {"center": v(445.84, 50) * mm, "radius": 2.5 * mm});
            skLineSegment(sketch, "E248.0", {"start": v(-108.16, 905) * mm, "end": v(-108.16, 805) * mm});
            skLineSegment(sketch, "E249", {"start": v(-108.16, 855) * mm, "end": v(-142.16, 855) * mm, "construction": true});
            skLineSegment(sketch, "E250", {"start": v(-108.16, 855) * mm, "end": v(445.84, 855) * mm, "construction": true});
            skCircle(sketch, "E251", {"center": v(-142.16, 855) * mm, "radius": 2.5 * mm});
            skCircle(sketch, "E252", {"center": v(445.84, 855) * mm, "radius": 2.5 * mm});
            skLineSegment(sketch, "E253.0", {"start": v(-142.16, 927) * mm, "end": v(-142.16, 915) * mm});
            skLineSegment(sketch, "E254", {"start": v(-142.16, 921) * mm, "end": v(445.84, 921) * mm, "construction": true});
            skLineSegment(sketch, "E255.0", {"start": v(-142.16, 1218) * mm, "end": v(-142.16, 1206) * mm});
            skLineSegment(sketch, "E256", {"start": v(-142.16, 1212) * mm, "end": v(445.84, 1212) * mm, "construction": true});
            skLineSegment(sketch, "E257.0", {"start": v(-142.16, 1300) * mm, "end": v(-142.16, 1288) * mm, "construction": true});
            skLineSegment(sketch, "E258", {"start": v(-142.16, 1294) * mm, "end": v(445.84, 1294) * mm, "construction": true});
            skCircle(sketch, "E259", {"center": v(48.5, 1212) * mm, "radius": 2.5 * mm});
            skCircle(sketch, "E260", {"center": v(255.17, 1212) * mm, "radius": 2.5 * mm});
            skCircle(sketch, "E261", {"center": v(48.5, 921) * mm, "radius": 2.5 * mm});
            skCircle(sketch, "E262", {"center": v(255.17, 921) * mm, "radius": 2.5 * mm});
            skCircle(sketch, "E263", {"center": v(255.17, 1294) * mm, "radius": 2.5 * mm});
            skCircle(sketch, "E264", {"center": v(48.5, 1294) * mm, "radius": 2.5 * mm});
            skLineSegment(sketch, "E265", {"start": v(465.2, 489) * mm, "end": v(465.2, 407) * mm, "construction": true});
            skLineSegment(sketch, "E266", {"start": v(465.2, 407) * mm, "end": v(465.2, 116) * mm, "construction": true});
            skLineSegment(sketch, "E267", {"start": v(465.2, 261.5) * mm, "end": v(-142.16, 261.5) * mm, "construction": true});
            skLineSegment(sketch, "E268", {"start": v(465.2, 261.5) * mm, "end": v(840.9, 261.5) * mm, "construction": true});
            skCircle(sketch, "E269", {"center": v(-142.16, 261.5) * mm, "radius": 2.5 * mm});
            skCircle(sketch, "E270", {"center": v(445.84, 261.5) * mm, "radius": 2.5 * mm});
            skLineSegment(sketch, "E271", {"start": v(465.2, 448) * mm, "end": v(-142.16, 448) * mm, "construction": true});
            skLineSegment(sketch, "E272", {"start": v(465.2, 448) * mm, "end": v(840.9, 448) * mm, "construction": true});
            skCircle(sketch, "E273", {"center": v(-142.16, 448) * mm, "radius": 2.5 * mm});
            skCircle(sketch, "E274", {"center": v(445.84, 448) * mm, "radius": 2.5 * mm});
            skLineSegment(sketch, "E275", {"start": v(510.9, -18.27) * mm, "end": v(516.9, -18.27) * mm, "construction": true});
            skLineSegment(sketch, "E276", {"start": v(516.9, -18.27) * mm, "end": v(516.9, 489) * mm, "construction": true});
            skLineSegment(sketch, "E277", {"start": v(840.9, -18.27) * mm, "end": v(834.9, -18.27) * mm, "construction": true});
            skLineSegment(sketch, "E278", {"start": v(834.9, -18.27) * mm, "end": v(834.9, 489) * mm, "construction": true});
            skLineSegment(sketch, "E279", {"start": v(465.2, 489) * mm, "end": v(465.2, 921) * mm, "construction": true});
            skLineSegment(sketch, "E280", {"start": v(465.2, 921) * mm, "end": v(465.2, 1212) * mm, "construction": true});
            skLineSegment(sketch, "E281", {"start": v(465.2, 1066.5) * mm, "end": v(-142.16, 1066.5) * mm, "construction": true});
            skLineSegment(sketch, "E282", {"start": v(465.2, 1212) * mm, "end": v(465.2, 1294) * mm, "construction": true});
            skLineSegment(sketch, "E283", {"start": v(465.2, 1253) * mm, "end": v(-142.16, 1253) * mm, "construction": true});
            skCircle(sketch, "E284", {"center": v(-142.16, 1253) * mm, "radius": 2.5 * mm});
            skCircle(sketch, "E285", {"center": v(445.84, 1253) * mm, "radius": 2.5 * mm});
            skCircle(sketch, "E286", {"center": v(445.84, 1066.5) * mm, "radius": 2.5 * mm});
            skCircle(sketch, "E287", {"center": v(-142.16, 1066.5) * mm, "radius": 2.5 * mm});
            skLineSegment(sketch, "E288.0", {"start": v(-136.16, 505) * mm, "end": v(-136.16, 0) * mm});
            skLineSegment(sketch, "E289", {"start": v(-136.16, 408.93) * mm, "end": v(-136.16, 505) * mm, "construction": true});
            skLineSegment(sketch, "E290", {"start": v(-136.16, 408.93) * mm, "end": v(-96.16, 408.93) * mm, "construction": true});
            skLineSegment(sketch, "E291", {"start": v(-142.16, 483) * mm, "end": v(-165.53, 483) * mm, "construction": true});
            skLineSegment(sketch, "E292", {"start": v(-165.53, 483) * mm, "end": v(-165.53, 451) * mm, "construction": true});
            skLineSegment(sketch, "E293", {"start": v(516.9, 489) * mm, "end": v(516.9, 424.41) * mm, "construction": true});
            skLineSegment(sketch, "E294", {"start": v(834.9, 489) * mm, "end": v(834.9, 424.41) * mm, "construction": true});
            skLineSegment(sketch, "E295.0", {"start": v(-136.16, 990.33) * mm, "end": v(-136.16, 1310) * mm, "construction": true});
            skLineSegment(sketch, "E296.0", {"start": v(439.84, 990.33) * mm, "end": v(439.84, 1310) * mm, "construction": true});
            skLineSegment(sketch, "E297", {"start": v(-96.16, 1183.53) * mm, "end": v(-136.16, 1183.53) * mm, "construction": true});
            skLineSegment(sketch, "E298", {"start": v(-136.16, 1183.53) * mm, "end": v(-136.16, 990.33) * mm, "construction": true});
            skLineSegment(sketch, "E299", {"start": v(399.84, 1198.1) * mm, "end": v(439.84, 1198.1) * mm, "construction": true});
            skLineSegment(sketch, "E300", {"start": v(439.84, 1198.1) * mm, "end": v(439.84, 990.33) * mm, "construction": true});
            skCircle(sketch, "E301", {"center": v(-96.16, 436) * mm, "radius": 22.5 * mm, "construction": true});
            skCircle(sketch, "E302", {"center": v(399.84, 436) * mm, "radius": 22.5 * mm, "construction": true});
            skCircle(sketch, "E303", {"center": v(556.9, 451) * mm, "radius": 22.5 * mm, "construction": true});
            skCircle(sketch, "E304", {"center": v(794.9, 451) * mm, "radius": 22.5 * mm, "construction": true});
            skCircle(sketch, "E305", {"center": v(399.84, 1241) * mm, "radius": 22.5 * mm, "construction": true});
            skCircle(sketch, "E306", {"center": v(-96.16, 1241) * mm, "radius": 22.5 * mm, "construction": true});
            skCircle(sketch, "E307", {"center": v(-115.64, 447.25) * mm, "radius": 3.3 * mm});
            skLineSegment(sketch, "E308", {"start": v(556.9, 436) * mm, "end": v(556.9, 428.5) * mm, "construction": true});
            skLineSegment(sketch, "E309", {"start": v(794.9, 436) * mm, "end": v(794.9, 428.5) * mm, "construction": true});
            skCircle(sketch, "E310", {"center": v(-115.64, 1252.25) * mm, "radius": 3.3 * mm});
            skCircle(sketch, "E311", {"center": v(-76.67, 1229.75) * mm, "radius": 3.3 * mm});
            skCircle(sketch, "E312", {"center": v(380.36, 1229.75) * mm, "radius": 3.3 * mm});
            skCircle(sketch, "E313", {"center": v(419.33, 1252.25) * mm, "radius": 3.3 * mm});
            skCircle(sketch, "E314", {"center": v(380.36, 424.75) * mm, "radius": 3.3 * mm});
            skCircle(sketch, "E315", {"center": v(419.33, 447.25) * mm, "radius": 3.3 * mm});
            skCircle(sketch, "E316", {"center": v(-76.67, 424.75) * mm, "radius": 3.3 * mm});
            skCircle(sketch, "E317", {"center": v(556.9, 473.5) * mm, "radius": 3.3 * mm});
            skCircle(sketch, "E318", {"center": v(556.9, 428.5) * mm, "radius": 3.3 * mm});
            skCircle(sketch, "E319", {"center": v(794.9, 428.5) * mm, "radius": 3.3 * mm});
            skCircle(sketch, "E320", {"center": v(794.9, 473.5) * mm, "radius": 3.3 * mm});
            skLineSegment(sketch, "E321.0", {"start": v(840.9, 401) * mm, "end": v(510.9, 401) * mm});
            skLineSegment(sketch, "E322.0", {"start": v(840.9, 122) * mm, "end": v(510.9, 122) * mm});
            skLineSegment(sketch, "E323", {"start": v(707.37, 401) * mm, "end": v(840.9, 401) * mm, "construction": true});
            skLineSegment(sketch, "E324", {"start": v(707.37, 122) * mm, "end": v(840.9, 122) * mm, "construction": true});
            skLineSegment(sketch, "E325", {"start": v(707.37, 391) * mm, "end": v(510.9, 391) * mm, "construction": true});
            skLineSegment(sketch, "E326", {"start": v(707.37, 132) * mm, "end": v(510.9, 132) * mm, "construction": true});
            skLineSegment(sketch, "E327", {"start": v(675.9, 401) * mm, "end": v(675.9, 122) * mm, "construction": true});
            skCircle(sketch, "E328", {"center": v(665.9, 272.52) * mm, "radius": 16 * mm, "construction": true});
            skCircle(sketch, "E329", {"center": v(685.9, 278.19) * mm, "radius": 16 * mm, "construction": true});
            skLineSegment(sketch, "E330", {"start": v(685.9, 278.19) * mm, "end": v(669.9, 278.19) * mm, "construction": true});
            skLineSegment(sketch, "E331", {"start": v(665.9, 272.52) * mm, "end": v(681.9, 272.52) * mm, "construction": true});
            skLineSegment(sketch, "E332", {"start": v(669.9, 391) * mm, "end": v(669.9, 278.19) * mm, "construction": true});
            skLineSegment(sketch, "E333", {"start": v(669.9, 278.19) * mm, "end": v(669.9, 132) * mm, "construction": true});
            skLineSegment(sketch, "E334", {"start": v(681.9, 272.52) * mm, "end": v(681.9, 391) * mm, "construction": true});
            skLineSegment(sketch, "E335", {"start": v(681.9, 272.52) * mm, "end": v(681.9, 132) * mm, "construction": true});
            skLineSegment(sketch, "E336", {"start": v(707.37, 401) * mm, "end": v(707.37, 391) * mm, "construction": true});
            skLineSegment(sketch, "E337", {"start": v(707.37, 132) * mm, "end": v(707.37, 122) * mm, "construction": true});
            skCircle(sketch, "E338", {"center": v(669.9, 391) * mm, "radius": 2.5 * mm});
            skCircle(sketch, "E339", {"center": v(681.9, 391) * mm, "radius": 2.5 * mm});
            skCircle(sketch, "E340", {"center": v(681.9, 132) * mm, "radius": 2.5 * mm});
            skCircle(sketch, "E341", {"center": v(669.9, 132) * mm, "radius": 2.5 * mm});
            skLineSegment(sketch, "E342", {"start": v(701.9, 278.19) * mm, "end": v(701.9, 391) * mm, "construction": true});
            skLineSegment(sketch, "E343", {"start": v(701.9, 278.19) * mm, "end": v(701.9, 132) * mm, "construction": true});
            skLineSegment(sketch, "E344", {"start": v(649.9, 272.52) * mm, "end": v(649.9, 132) * mm, "construction": true});
            skLineSegment(sketch, "E345", {"start": v(649.9, 272.52) * mm, "end": v(649.9, 391) * mm, "construction": true});
            skCircle(sketch, "E346", {"center": v(701.9, 391) * mm, "radius": 2.5 * mm});
            skCircle(sketch, "E347", {"center": v(649.9, 391) * mm, "radius": 2.5 * mm});
            skCircle(sketch, "E348", {"center": v(701.9, 132) * mm, "radius": 2.5 * mm});
            skCircle(sketch, "E349", {"center": v(649.9, 132) * mm, "radius": 2.5 * mm});
            skLineSegment(sketch, "E350.0", {"start": v(-142.16, -135.27) * mm, "end": v(-142.16, -465.27) * mm});
            skLineSegment(sketch, "E351", {"start": v(-142.16, -290.27) * mm, "end": v(445.84, -290.27) * mm, "construction": true});
            skCircle(sketch, "E352", {"center": v(151.84, -290.27) * mm, "radius": 16 * mm, "construction": true});
            skLineSegment(sketch, "E353", {"start": v(151.84, -290.27) * mm, "end": v(151.84, -274.27) * mm, "construction": true});
            skLineSegment(sketch, "E354", {"start": v(151.84, -290.27) * mm, "end": v(151.84, -306.27) * mm, "construction": true});
            skLineSegment(sketch, "E355", {"start": v(151.84, -274.27) * mm, "end": v(-142.16, -274.27) * mm, "construction": true});
            skLineSegment(sketch, "E356", {"start": v(151.84, -306.27) * mm, "end": v(-142.16, -306.27) * mm, "construction": true});
            skLineSegment(sketch, "E357", {"start": v(151.84, -274.27) * mm, "end": v(445.84, -274.27) * mm, "construction": true});
            skLineSegment(sketch, "E358", {"start": v(151.84, -306.27) * mm, "end": v(445.84, -306.27) * mm, "construction": true});
            skLineSegment(sketch, "E359.0", {"start": v(-226.54, -215.82) * mm, "end": v(-222.46, -227.77) * mm, "construction": true});
            skCircle(sketch, "E360.0", {"center": v(-242.15, -243.65) * mm, "radius": 18 * mm, "construction": true});
            skLineSegment(sketch, "E361.0", {"start": v(-237.74, -215.82) * mm, "end": v(-241.83, -227.77) * mm, "construction": true});
            skCircle(sketch, "E362.0", {"center": v(-242.15, -221.32) * mm, "radius": 3.25 * mm, "construction": true});
            skCircle(sketch, "E363.0", {"center": v(-242.15, -252.15) * mm, "radius": 3.25 * mm, "construction": true});
            skLineSegment(sketch, "E364.0", {"start": v(-226.54, -271.48) * mm, "end": v(-222.46, -259.54) * mm, "construction": true});
            skLineSegment(sketch, "E365.0", {"start": v(-237.74, -271.48) * mm, "end": v(-241.83, -259.54) * mm, "construction": true});
            skCircle(sketch, "E366.0", {"center": v(-232.14, -243.65) * mm, "radius": 5 * mm, "construction": true});
            skLineSegment(sketch, "E367.0", {"start": v(-148.16, -23.84) * mm, "end": v(-136.16, -23.84) * mm});
            skLineSegment(sketch, "E368.1", {"start": v(451.84, -23.84) * mm, "end": v(439.84, -23.84) * mm});
            skLineSegment(sketch, "E369", {"start": v(-136.16, -23.84) * mm, "end": v(-136.16, -931.36) * mm, "construction": true});
            skLineSegment(sketch, "E370", {"start": v(439.84, -23.84) * mm, "end": v(439.84, -931.36) * mm, "construction": true});
            skLineSegment(sketch, "E371", {"start": v(-242.15, -243.65) * mm, "end": v(-210.22, -243.65) * mm, "construction": true});
            skLineSegment(sketch, "E372", {"start": v(-242.15, -243.65) * mm, "end": v(-242.15, -221.32) * mm, "construction": true});
            skLineSegment(sketch, "E373", {"start": v(-242.15, -243.65) * mm, "end": v(-242.15, -252.15) * mm, "construction": true});
            skLineSegment(sketch, "E374", {"start": v(-245.21, -213.81) * mm, "end": v(-239.08, -213.81) * mm, "construction": true});
            skLineSegment(sketch, "E375", {"start": v(-245.21, -259.49) * mm, "end": v(-239.08, -260.5) * mm, "construction": true});
            skLineSegment(sketch, "E376", {"start": v(-241.83, -227.77) * mm, "end": v(-241.83, -259.54) * mm, "construction": true});
            skLineSegment(sketch, "E377", {"start": v(-222.46, -227.77) * mm, "end": v(-222.46, -259.54) * mm, "construction": true});
            skLineSegment(sketch, "E378", {"start": v(-241.83, -243.65) * mm, "end": v(-242.15, -243.65) * mm, "construction": true});
            skLineSegment(sketch, "E379", {"start": v(-237.74, -215.82) * mm, "end": v(-237.74, -271.48) * mm, "construction": true});
            skLineSegment(sketch, "E380", {"start": v(-226.54, -215.82) * mm, "end": v(-226.54, -271.48) * mm, "construction": true});
            skLineSegment(sketch, "E381", {"start": v(-242.15, -213.81) * mm, "end": v(-242.15, -221.32) * mm, "construction": true});
            skLineSegment(sketch, "E382", {"start": v(-242.15, -252.15) * mm, "end": v(-242.15, -260) * mm, "construction": true});
            skCircle(sketch, "E383", {"center": v(-242.15, -243.65) * mm, "radius": 22.33 * mm, "construction": true});
            skCircle(sketch, "E384", {"center": v(-116.16, -250.27) * mm, "radius": 30 * mm, "construction": true});
            skCircle(sketch, "E385", {"center": v(-116.16, -250.27) * mm, "radius": 18.25 * mm, "construction": true});
            skLineSegment(sketch, "E386", {"start": v(-116.16, -250.27) * mm, "end": v(-116.16, -280.27) * mm, "construction": true});
            skLineSegment(sketch, "E387", {"start": v(-116.16, -250.27) * mm, "end": v(-121.37, -220.73) * mm, "construction": true});
            skLineSegment(sketch, "E388", {"start": v(-116.16, -250.27) * mm, "end": v(-110.95, -279.82) * mm, "construction": true});
            skCircle(sketch, "E389", {"center": v(-119.33, -232.3) * mm, "radius": 2.5 * mm});
            skCircle(sketch, "E390", {"center": v(-112.99, -268.25) * mm, "radius": 2.5 * mm});
            skLineSegment(sketch, "E391", {"start": v(-116.16, -280.27) * mm, "end": v(-116.16, -290.27) * mm, "construction": true});
            skLineSegment(sketch, "E392", {"start": v(-136.16, -282.47) * mm, "end": v(-116.16, -282.47) * mm, "construction": true});
            skCircle(sketch, "E393", {"center": v(-116.16, -250.27) * mm, "radius": 5 * mm});
            skLineSegment(sketch, "E394", {"start": v(439.84, -290.27) * mm, "end": v(419.84, -290.27) * mm, "construction": true});
            skCircle(sketch, "E395", {"center": v(416.67, -312.3) * mm, "radius": 2.5 * mm});
            skCircle(sketch, "E396", {"center": v(419.84, -330.27) * mm, "radius": 5 * mm});
            skCircle(sketch, "E397", {"center": v(423.01, -348.25) * mm, "radius": 2.5 * mm});
            skCircle(sketch, "E398", {"center": v(419.84, -330.27) * mm, "radius": 18.25 * mm, "construction": true});
            skLineSegment(sketch, "E399", {"start": v(419.84, -330.27) * mm, "end": v(419.84, -312.02) * mm, "construction": true});
            skLineSegment(sketch, "E400", {"start": v(416.67, -312.3) * mm, "end": v(419.84, -330.27) * mm, "construction": true});
            skLineSegment(sketch, "E401", {"start": v(423.01, -348.25) * mm, "end": v(419.84, -330.27) * mm, "construction": true});
            skLineSegment(sketch, "E402", {"start": v(419.84, -290.27) * mm, "end": v(419.84, -300.27) * mm, "construction": true});
            skLineSegment(sketch, "E403", {"start": v(419.84, -300.27) * mm, "end": v(419.84, -330.27) * mm, "construction": true});
            skLineSegment(sketch, "E404", {"start": v(419.84, -312.02) * mm, "end": v(416.67, -312.3) * mm, "construction": true});
            skLineSegment(sketch, "E405", {"start": v(419.84, -653.35) * mm, "end": v(419.84, -683.35) * mm, "construction": true});
            skLineSegment(sketch, "E406", {"start": v(419.84, -643.35) * mm, "end": v(419.84, -653.35) * mm, "construction": true});
            skCircle(sketch, "E407", {"center": v(423.01, -701.32) * mm, "radius": 2.5 * mm});
            skCircle(sketch, "E408", {"center": v(416.67, -665.38) * mm, "radius": 2.5 * mm});
            skLineSegment(sketch, "E409", {"start": v(419.84, -665.1) * mm, "end": v(416.67, -665.38) * mm, "construction": true});
            skCircle(sketch, "E410", {"center": v(419.84, -683.35) * mm, "radius": 18.25 * mm, "construction": true});
            skCircle(sketch, "E411", {"center": v(419.84, -683.35) * mm, "radius": 5 * mm});
            skLineSegment(sketch, "E412", {"start": v(439.84, -643.35) * mm, "end": v(419.84, -643.35) * mm, "construction": true});
            skLineSegment(sketch, "E413", {"start": v(423.01, -701.32) * mm, "end": v(419.84, -683.35) * mm, "construction": true});
            skLineSegment(sketch, "E414", {"start": v(416.67, -665.38) * mm, "end": v(419.84, -683.35) * mm, "construction": true});
            skLineSegment(sketch, "E415", {"start": v(419.84, -683.35) * mm, "end": v(419.84, -665.1) * mm, "construction": true});
            skLineSegment(sketch, "E416.0", {"start": v(445.84, -643.35) * mm, "end": v(355.84, -643.35) * mm, "construction": true});
            skLineSegment(sketch, "E417", {"start": v(439.84, -643.35) * mm, "end": v(445.84, -643.35) * mm, "construction": true});
            skLineSegment(sketch, "E418", {"start": v(-116.16, -603.35) * mm, "end": v(-116.16, -585.1) * mm, "construction": true});
            skLineSegment(sketch, "E419", {"start": v(-112.99, -621.32) * mm, "end": v(-116.16, -603.35) * mm, "construction": true});
            skLineSegment(sketch, "E420", {"start": v(-119.33, -585.38) * mm, "end": v(-116.16, -603.35) * mm, "construction": true});
            skCircle(sketch, "E421", {"center": v(-116.16, -603.35) * mm, "radius": 5 * mm});
            skCircle(sketch, "E422", {"center": v(-116.16, -603.35) * mm, "radius": 18.25 * mm, "construction": true});
            skLineSegment(sketch, "E423", {"start": v(-116.16, -585.1) * mm, "end": v(-119.33, -585.38) * mm, "construction": true});
            skCircle(sketch, "E424", {"center": v(-112.99, -621.32) * mm, "radius": 2.5 * mm});
            skCircle(sketch, "E425", {"center": v(-119.33, -585.38) * mm, "radius": 2.5 * mm});
            skLineSegment(sketch, "E426", {"start": v(-116.16, -573.35) * mm, "end": v(-116.16, -603.35) * mm, "construction": true});
            skLineSegment(sketch, "E427", {"start": v(-116.16, -643.35) * mm, "end": v(-136.16, -643.35) * mm, "construction": true});
            skLineSegment(sketch, "E428", {"start": v(-136.16, -643.35) * mm, "end": v(-142.16, -643.35) * mm, "construction": true});
            skLineSegment(sketch, "E429", {"start": v(-116.16, -643.35) * mm, "end": v(-116.16, -633.35) * mm, "construction": true});
            skLineSegment(sketch, "E430", {"start": v(-116.16, -603.35) * mm, "end": v(-116.16, -633.35) * mm, "construction": true});
            skLineSegment(sketch, "E431", {"start": v(-112.99, -268.25) * mm, "end": v(-116.16, -268.52) * mm, "construction": true});
            skCircle(sketch, "E432", {"center": v(419.84, -290.27) * mm, "radius": 6 * mm});
            skCircle(sketch, "E433", {"center": v(-116.16, -290.27) * mm, "radius": 6 * mm});
            skCircle(sketch, "E434", {"center": v(-116.16, -643.35) * mm, "radius": 6 * mm});
            skCircle(sketch, "E435", {"center": v(419.84, -643.35) * mm, "radius": 6 * mm});
            skLineSegment(sketch, "E436", {"start": v(285.93, -643.35) * mm, "end": v(285.93, -818.35) * mm, "construction": true});
            skLineSegment(sketch, "E437.0", {"start": v(-142.16, -818.35) * mm, "end": v(445.84, -818.35) * mm, "construction": true});
            skLineSegment(sketch, "E438.0", {"start": v(-142.16, -465.27) * mm, "end": v(445.84, -465.27) * mm});
            skLineSegment(sketch, "E439", {"start": v(64.15, -290.27) * mm, "end": v(64.15, -465.27) * mm, "construction": true});
            skLineSegment(sketch, "E440", {"start": v(-119.33, -232.3) * mm, "end": v(-136.16, -232.3) * mm, "construction": true});
            skLineSegment(sketch, "E441", {"start": v(423.01, -348.25) * mm, "end": v(439.84, -348.25) * mm, "construction": true});
            skLineSegment(sketch, "E442", {"start": v(685.9, 278.19) * mm, "end": v(510.9, 278.19) * mm, "construction": true});
            skLineSegment(sketch, "E443", {"start": v(665.9, 272.52) * mm, "end": v(840.9, 272.52) * mm, "construction": true});
            skLineSegment(sketch, "E444", {"start": v(665.9, 272.52) * mm, "end": v(649.9, 272.52) * mm, "construction": true});
            skLineSegment(sketch, "E445", {"start": v(685.9, 278.19) * mm, "end": v(701.9, 278.19) * mm, "construction": true});
            skLineSegment(sketch, "E446", {"start": v(380.36, 1229.75) * mm, "end": v(419.33, 1252.25) * mm, "construction": true});
            skLineSegment(sketch, "E447", {"start": v(-115.64, 1252.25) * mm, "end": v(-76.67, 1229.75) * mm, "construction": true});
            skLineSegment(sketch, "E448", {"start": v(380.36, 424.75) * mm, "end": v(419.33, 447.25) * mm, "construction": true});
            skLineSegment(sketch, "E449", {"start": v(-115.64, 447.25) * mm, "end": v(-76.67, 424.75) * mm, "construction": true});
            skSolve(sketch);
        }
        {
            var Q0;
            Q0=qSketchRegion(id+"F3",true);
            extrude(context, id + "F4", {"entities" : qUnion([Q0]), "operationType" : NewBodyOperationType.REMOVE, "oppositeDirection" : true, "depth" : 25 * mm});
        }
        {
            var Q0;
            Q0=makeQuery(id+"F1.opExtrude","SWEPT_EDGE",EDGE,{"disambiguationData":[OSD([sQuery(id+"F0.wireOp",EDGE,"E0.top"),sQuery(id+"F0.wireOp",EDGE,"E0.right")])]});
            var Q1;
            Q1=makeQuery(id+"F1.opExtrude","SWEPT_EDGE",EDGE,{"disambiguationData":[OSD([sQuery(id+"F0.wireOp",EDGE,"E0.top"),sQuery(id+"F0.wireOp",EDGE,"E0.left")])]});
            var Q2;
            Q2=makeQuery(id+"F1.opExtrude","SWEPT_EDGE",EDGE,{"disambiguationData":[OSD([sQuery(id+"F0.wireOp",EDGE,"E29"),sQuery(id+"F0.wireOp",EDGE,"E30")])]});
            var Q3;
            Q3=makeQuery(id+"F1.opExtrude","SWEPT_EDGE",EDGE,{"disambiguationData":[OSD([sQuery(id+"F0.wireOp",EDGE,"E28"),sQuery(id+"F0.wireOp",EDGE,"E29")])]});
            var Q4;
            Q4=makeQuery(id+"F1.opExtrude","SWEPT_EDGE",EDGE,{"disambiguationData":[OSD([sQuery(id+"F0.wireOp",EDGE,"E28"),sQuery(id+"F0.wireOp",EDGE,"E35")])]});
            var Q5;
            Q5=makeQuery(id+"F1.opExtrude","SWEPT_EDGE",EDGE,{"disambiguationData":[OSD([sQuery(id+"F0.wireOp",EDGE,"E34"),sQuery(id+"F0.wireOp",EDGE,"E35")])]});
            var Q6;
            Q6=makeQuery(id+"F1.opExtrude","SWEPT_EDGE",EDGE,{"disambiguationData":[OSD([sQuery(id+"F0.wireOp",EDGE,"E30"),sQuery(id+"F0.wireOp",EDGE,"E31")])]});
            var Q7;
            Q7=makeQuery(id+"F1.opExtrude","SWEPT_EDGE",EDGE,{"disambiguationData":[OSD([sQuery(id+"F0.wireOp",EDGE,"E31"),sQuery(id+"F0.wireOp",EDGE,"E32")])]});
            var Q8;
            Q8=makeQuery(id+"F1.opExtrude","SWEPT_EDGE",EDGE,{"disambiguationData":[OSD([sQuery(id+"F0.wireOp",EDGE,"E20"),sQuery(id+"F0.wireOp",EDGE,"E21")])]});
            var Q9;
            Q9=makeQuery(id+"F1.opExtrude","SWEPT_EDGE",EDGE,{"disambiguationData":[OSD([sQuery(id+"F0.wireOp",EDGE,"E17"),sQuery(id+"F0.wireOp",EDGE,"E18")])]});
            var Q10;
            Q10=makeQuery(id+"F1.opExtrude","SWEPT_EDGE",EDGE,{"disambiguationData":[OSD([sQuery(id+"F0.wireOp",EDGE,"E4"),sQuery(id+"F0.wireOp",EDGE,"E5")])]});
            var Q11;
            Q11=makeQuery(id+"F1.opExtrude","SWEPT_EDGE",EDGE,{"disambiguationData":[OSD([sQuery(id+"F0.wireOp",EDGE,"E1"),sQuery(id+"F0.wireOp",EDGE,"E2")])]});
            var Q12;
            Q12=makeQuery(id+"F1.opExtrude","SWEPT_EDGE",EDGE,{"disambiguationData":[OSD([sQuery(id+"F0.wireOp",EDGE,"E0.left"),sQuery(id+"F0.wireOp",EDGE,"E1")])]});
            var Q13;
            Q13=makeQuery(id+"F1.opExtrude","SWEPT_EDGE",EDGE,{"disambiguationData":[OSD([sQuery(id+"F0.wireOp",EDGE,"E0.right"),sQuery(id+"F0.wireOp",EDGE,"E5")])]});
            fillet(context, id + "F5", {"entities" : qUnion([Q0, Q1, Q2, Q3, Q4, Q5, Q6, Q7, Q8, Q9, Q10, Q11, Q12, Q13]), "radius" : 7 * mm, "tangentPropagation" : true, "allowEdgeOverflow" : false});
        }
        {
            var Q0;
            Q0=qCreatedBy(makeId("Top.planeOp"),FACE);
            var sketch = newSketch(context, id + "F6", { "sketchPlane" : qUnion([Q0])});
            skCircle(sketch, "E450", {"center": v(569.82, -353.66) * mm, "radius": 1.5 * mm});
            skCircle(sketch, "E451", {"center": v(569.82, -323.66) * mm, "radius": 1.5 * mm});
            skCircle(sketch, "E452", {"center": v(539.82, -353.66) * mm, "radius": 1.5 * mm});
            skLineSegment(sketch, "E453", {"start": v(539.82, -353.66) * mm, "end": v(539.82, -338.66) * mm, "construction": true});
            skLineSegment(sketch, "E454", {"start": v(554.82, -353.66) * mm, "end": v(539.82, -353.66) * mm, "construction": true});
            skLineSegment(sketch, "E455", {"start": v(539.82, -338.66) * mm, "end": v(539.82, -323.66) * mm, "construction": true});
            skLineSegment(sketch, "E456.top", {"start": v(533.82, -359.66) * mm, "end": v(575.82, -359.66) * mm});
            skLineSegment(sketch, "E456.bottom", {"start": v(533.82, -317.66) * mm, "end": v(575.82, -317.66) * mm});
            skLineSegment(sketch, "E456.right", {"start": v(575.82, -317.66) * mm, "end": v(575.82, -359.66) * mm});
            skLineSegment(sketch, "E456.left", {"start": v(533.82, -317.66) * mm, "end": v(533.82, -359.66) * mm});
            skLineSegment(sketch, "E457", {"start": v(569.82, -353.66) * mm, "end": v(554.82, -353.66) * mm, "construction": true});
            skLineSegment(sketch, "E458", {"start": v(569.82, -338.66) * mm, "end": v(569.82, -353.66) * mm, "construction": true});
            skLineSegment(sketch, "E459", {"start": v(533.82, -338.66) * mm, "end": v(575.82, -338.66) * mm, "construction": true});
            skLineSegment(sketch, "E460", {"start": v(554.82, -317.66) * mm, "end": v(554.82, -359.66) * mm, "construction": true});
            skCircle(sketch, "E461", {"center": v(554.82, -338.66) * mm, "radius": 11 * mm});
            skLineSegment(sketch, "E462", {"start": v(539.82, -323.66) * mm, "end": v(554.82, -323.66) * mm, "construction": true});
            skCircle(sketch, "E463", {"center": v(554.82, -338.66) * mm, "radius": 2.5 * mm});
            skLineSegment(sketch, "E464", {"start": v(569.82, -323.66) * mm, "end": v(569.82, -338.66) * mm, "construction": true});
            skLineSegment(sketch, "E465", {"start": v(554.82, -323.66) * mm, "end": v(569.82, -323.66) * mm, "construction": true});
            skCircle(sketch, "E466", {"center": v(539.82, -323.66) * mm, "radius": 1.5 * mm});
            skCircle(sketch, "E467", {"center": v(434.84, -345.27) * mm, "radius": 1.5 * mm});
            skCircle(sketch, "E468", {"center": v(434.84, -315.27) * mm, "radius": 1.5 * mm});
            skCircle(sketch, "E469", {"center": v(404.84, -345.27) * mm, "radius": 1.5 * mm});
            skLineSegment(sketch, "E470", {"start": v(404.84, -345.27) * mm, "end": v(404.84, -330.27) * mm, "construction": true});
            skLineSegment(sketch, "E471", {"start": v(419.84, -345.27) * mm, "end": v(404.84, -345.27) * mm, "construction": true});
            skLineSegment(sketch, "E472", {"start": v(404.84, -330.27) * mm, "end": v(404.84, -315.27) * mm, "construction": true});
            skLineSegment(sketch, "E473.top", {"start": v(398.84, -351.27) * mm, "end": v(440.84, -351.27) * mm, "construction": true});
            skLineSegment(sketch, "E473.bottom", {"start": v(398.84, -309.27) * mm, "end": v(440.84, -309.27) * mm, "construction": true});
            skLineSegment(sketch, "E473.right", {"start": v(440.84, -309.27) * mm, "end": v(440.84, -351.27) * mm, "construction": true});
            skLineSegment(sketch, "E473.left", {"start": v(398.84, -309.27) * mm, "end": v(398.84, -351.27) * mm, "construction": true});
            skLineSegment(sketch, "E474", {"start": v(434.84, -345.27) * mm, "end": v(419.84, -345.27) * mm, "construction": true});
            skLineSegment(sketch, "E475", {"start": v(434.84, -330.27) * mm, "end": v(434.84, -345.27) * mm, "construction": true});
            skLineSegment(sketch, "E476", {"start": v(398.84, -330.27) * mm, "end": v(440.84, -330.27) * mm, "construction": true});
            skLineSegment(sketch, "E477", {"start": v(419.84, -309.27) * mm, "end": v(419.84, -351.27) * mm, "construction": true});
            skCircle(sketch, "E478", {"center": v(419.84, -330.27) * mm, "radius": 11 * mm, "construction": true});
            skLineSegment(sketch, "E479", {"start": v(404.84, -315.27) * mm, "end": v(419.84, -315.27) * mm, "construction": true});
            skCircle(sketch, "E480", {"center": v(419.84, -330.27) * mm, "radius": 2.5 * mm, "construction": true});
            skLineSegment(sketch, "E481", {"start": v(434.84, -315.27) * mm, "end": v(434.84, -330.27) * mm, "construction": true});
            skLineSegment(sketch, "E482", {"start": v(419.84, -315.27) * mm, "end": v(434.84, -315.27) * mm, "construction": true});
            skCircle(sketch, "E483", {"center": v(404.84, -315.27) * mm, "radius": 1.5 * mm});
            skLineSegment(sketch, "E484", {"start": v(-101.16, -265.27) * mm, "end": v(-116.16, -265.27) * mm, "construction": true});
            skLineSegment(sketch, "E485", {"start": v(-101.16, -235.27) * mm, "end": v(-101.16, -250.27) * mm, "construction": true});
            skLineSegment(sketch, "E486", {"start": v(-101.16, -250.27) * mm, "end": v(-101.16, -265.27) * mm, "construction": true});
            skCircle(sketch, "E487", {"center": v(-101.16, -235.27) * mm, "radius": 1.5 * mm});
            skLineSegment(sketch, "E488", {"start": v(-131.16, -250.27) * mm, "end": v(-131.16, -235.27) * mm, "construction": true});
            skLineSegment(sketch, "E489", {"start": v(-116.16, -265.27) * mm, "end": v(-131.16, -265.27) * mm, "construction": true});
            skLineSegment(sketch, "E490.right", {"start": v(-95.16, -229.27) * mm, "end": v(-95.16, -271.27) * mm, "construction": true});
            skLineSegment(sketch, "E491", {"start": v(-116.16, -229.27) * mm, "end": v(-116.16, -271.27) * mm, "construction": true});
            skCircle(sketch, "E492", {"center": v(-131.16, -235.27) * mm, "radius": 1.5 * mm});
            skLineSegment(sketch, "E493", {"start": v(-131.16, -265.27) * mm, "end": v(-131.16, -250.27) * mm, "construction": true});
            skCircle(sketch, "E494", {"center": v(-116.16, -250.27) * mm, "radius": 2.5 * mm, "construction": true});
            skLineSegment(sketch, "E490.left", {"start": v(-137.16, -229.27) * mm, "end": v(-137.16, -271.27) * mm, "construction": true});
            skLineSegment(sketch, "E490.bottom", {"start": v(-137.16, -229.27) * mm, "end": v(-95.16, -229.27) * mm, "construction": true});
            skLineSegment(sketch, "E495", {"start": v(-137.16, -250.27) * mm, "end": v(-95.16, -250.27) * mm, "construction": true});
            skLineSegment(sketch, "E496", {"start": v(-116.16, -235.27) * mm, "end": v(-101.16, -235.27) * mm, "construction": true});
            skCircle(sketch, "E497", {"center": v(-116.16, -250.27) * mm, "radius": 11 * mm, "construction": true});
            skLineSegment(sketch, "E490.top", {"start": v(-137.16, -271.27) * mm, "end": v(-95.16, -271.27) * mm, "construction": true});
            skLineSegment(sketch, "E498", {"start": v(-131.16, -235.27) * mm, "end": v(-116.16, -235.27) * mm, "construction": true});
            skCircle(sketch, "E499", {"center": v(-101.16, -265.27) * mm, "radius": 1.5 * mm});
            skCircle(sketch, "E500", {"center": v(-131.16, -265.27) * mm, "radius": 1.5 * mm});
            skLineSegment(sketch, "E501", {"start": v(-75.67, 441.5) * mm, "end": v(-83.17, 428.5) * mm, "construction": true});
            skLineSegment(sketch, "E502", {"start": v(-101.65, 456.5) * mm, "end": v(-88.66, 449) * mm, "construction": true});
            skLineSegment(sketch, "E503", {"start": v(-88.66, 449) * mm, "end": v(-75.67, 441.5) * mm, "construction": true});
            skCircle(sketch, "E504", {"center": v(-101.65, 456.5) * mm, "radius": 1.5 * mm});
            skLineSegment(sketch, "E505", {"start": v(-103.66, 423) * mm, "end": v(-116.65, 430.5) * mm, "construction": true});
            skLineSegment(sketch, "E506", {"start": v(-83.17, 428.5) * mm, "end": v(-90.67, 415.5) * mm, "construction": true});
            skLineSegment(sketch, "E507.right", {"start": v(-103.85, 464.69) * mm, "end": v(-67.47, 443.69) * mm, "construction": true});
            skLineSegment(sketch, "E508", {"start": v(-114.35, 446.5) * mm, "end": v(-77.97, 425.5) * mm, "construction": true});
            skCircle(sketch, "E509", {"center": v(-116.65, 430.5) * mm, "radius": 1.5 * mm});
            skLineSegment(sketch, "E510", {"start": v(-90.67, 415.5) * mm, "end": v(-103.66, 423) * mm, "construction": true});
            skCircle(sketch, "E511", {"center": v(-96.16, 436) * mm, "radius": 2.5 * mm, "construction": true});
            skLineSegment(sketch, "E507.left", {"start": v(-124.85, 428.31) * mm, "end": v(-88.47, 407.31) * mm, "construction": true});
            skLineSegment(sketch, "E507.bottom", {"start": v(-124.85, 428.31) * mm, "end": v(-103.85, 464.69) * mm, "construction": true});
            skLineSegment(sketch, "E512", {"start": v(-106.66, 417.81) * mm, "end": v(-85.66, 454.19) * mm, "construction": true});
            skLineSegment(sketch, "E513", {"start": v(-109.15, 443.5) * mm, "end": v(-101.65, 456.5) * mm, "construction": true});
            skCircle(sketch, "E514", {"center": v(-96.16, 436) * mm, "radius": 11 * mm, "construction": true});
            skLineSegment(sketch, "E507.top", {"start": v(-88.47, 407.31) * mm, "end": v(-67.47, 443.69) * mm, "construction": true});
            skLineSegment(sketch, "E515", {"start": v(-116.65, 430.5) * mm, "end": v(-109.15, 443.5) * mm, "construction": true});
            skCircle(sketch, "E516", {"center": v(-75.67, 441.5) * mm, "radius": 1.5 * mm});
            skCircle(sketch, "E517", {"center": v(-90.67, 415.5) * mm, "radius": 1.5 * mm});
            skLineSegment(sketch, "E518", {"start": v(809.9, 436) * mm, "end": v(794.9, 436) * mm, "construction": true});
            skLineSegment(sketch, "E519", {"start": v(809.9, 466) * mm, "end": v(809.9, 451) * mm, "construction": true});
            skLineSegment(sketch, "E520", {"start": v(809.9, 451) * mm, "end": v(809.9, 436) * mm, "construction": true});
            skCircle(sketch, "E521", {"center": v(809.9, 466) * mm, "radius": 1.5 * mm});
            skLineSegment(sketch, "E522", {"start": v(779.9, 451) * mm, "end": v(779.9, 466) * mm, "construction": true});
            skLineSegment(sketch, "E523", {"start": v(794.9, 436) * mm, "end": v(779.9, 436) * mm, "construction": true});
            skLineSegment(sketch, "E524.right", {"start": v(815.9, 472) * mm, "end": v(815.9, 430) * mm, "construction": true});
            skLineSegment(sketch, "E525", {"start": v(794.9, 472) * mm, "end": v(794.9, 430) * mm, "construction": true});
            skCircle(sketch, "E526", {"center": v(779.9, 466) * mm, "radius": 1.5 * mm});
            skLineSegment(sketch, "E527", {"start": v(779.9, 436) * mm, "end": v(779.9, 451) * mm, "construction": true});
            skCircle(sketch, "E528", {"center": v(794.9, 451) * mm, "radius": 2.5 * mm, "construction": true});
            skLineSegment(sketch, "E524.left", {"start": v(773.9, 472) * mm, "end": v(773.9, 430) * mm, "construction": true});
            skLineSegment(sketch, "E524.bottom", {"start": v(773.9, 472) * mm, "end": v(815.9, 472) * mm, "construction": true});
            skLineSegment(sketch, "E529", {"start": v(773.9, 451) * mm, "end": v(815.9, 451) * mm, "construction": true});
            skLineSegment(sketch, "E530", {"start": v(794.9, 466) * mm, "end": v(809.9, 466) * mm, "construction": true});
            skCircle(sketch, "E531", {"center": v(794.9, 451) * mm, "radius": 11 * mm, "construction": true});
            skLineSegment(sketch, "E524.top", {"start": v(773.9, 430) * mm, "end": v(815.9, 430) * mm, "construction": true});
            skLineSegment(sketch, "E532", {"start": v(779.9, 466) * mm, "end": v(794.9, 466) * mm, "construction": true});
            skCircle(sketch, "E533", {"center": v(809.9, 436) * mm, "radius": 1.5 * mm});
            skCircle(sketch, "E534", {"center": v(779.9, 436) * mm, "radius": 1.5 * mm});
            skLineSegment(sketch, "E535", {"start": v(-96.16, 436) * mm, "end": v(-56.25, 436) * mm, "construction": true});
            skSolve(sketch);
        }
        {
            var Q0;
            Q0=makeQuery(id+"F6.imprint","IMPRINT",FACE,{"disambiguationData":[TD([[makeQuery(id+"F6.imprint","IMPRINT",EDGE,{"derivedFrom":sQuery(id+"F6.wireOp",EDGE,"E509")}),1.0]])]});
            var Q1;
            Q1=makeQuery(id+"F6.imprint","IMPRINT",FACE,{"disambiguationData":[TD([[makeQuery(id+"F6.imprint","IMPRINT",EDGE,{"derivedFrom":sQuery(id+"F6.wireOp",EDGE,"E504")}),1.0]])]});
            var Q2;
            Q2=makeQuery(id+"F6.imprint","IMPRINT",FACE,{"disambiguationData":[TD([[makeQuery(id+"F6.imprint","IMPRINT",EDGE,{"derivedFrom":sQuery(id+"F6.wireOp",EDGE,"E517")}),1.0]])]});
            var Q3;
            Q3=makeQuery(id+"F6.imprint","IMPRINT",FACE,{"disambiguationData":[TD([[makeQuery(id+"F6.imprint","IMPRINT",EDGE,{"derivedFrom":sQuery(id+"F6.wireOp",EDGE,"E516")}),1.0]])]});
            var Q4;
            Q4=makeQuery(id+"F6.imprint","IMPRINT",FACE,{"disambiguationData":[TD([[makeQuery(id+"F6.imprint","IMPRINT",EDGE,{"derivedFrom":sQuery(id+"F6.wireOp",EDGE,"E526")}),1.0]])]});
            var Q5;
            Q5=makeQuery(id+"F6.imprint","IMPRINT",FACE,{"disambiguationData":[TD([[makeQuery(id+"F6.imprint","IMPRINT",EDGE,{"derivedFrom":sQuery(id+"F6.wireOp",EDGE,"E534")}),1.0]])]});
            var Q6;
            Q6=makeQuery(id+"F6.imprint","IMPRINT",FACE,{"disambiguationData":[TD([[makeQuery(id+"F6.imprint","IMPRINT",EDGE,{"derivedFrom":sQuery(id+"F6.wireOp",EDGE,"E533")}),1.0]])]});
            var Q7;
            Q7=makeQuery(id+"F6.imprint","IMPRINT",FACE,{"disambiguationData":[TD([[makeQuery(id+"F6.imprint","IMPRINT",EDGE,{"derivedFrom":sQuery(id+"F6.wireOp",EDGE,"E521")}),1.0]])]});
            var Q8;
            Q8=makeQuery(id+"F6.imprint","IMPRINT",FACE,{"disambiguationData":[TD([[makeQuery(id+"F6.imprint","IMPRINT",EDGE,{"derivedFrom":sQuery(id+"F6.wireOp",EDGE,"E499")}),1.0]])]});
            var Q9;
            Q9=makeQuery(id+"F6.imprint","IMPRINT",FACE,{"disambiguationData":[TD([[makeQuery(id+"F6.imprint","IMPRINT",EDGE,{"derivedFrom":sQuery(id+"F6.wireOp",EDGE,"E500")}),1.0]])]});
            var Q10;
            Q10=makeQuery(id+"F6.imprint","IMPRINT",FACE,{"disambiguationData":[TD([[makeQuery(id+"F6.imprint","IMPRINT",EDGE,{"derivedFrom":sQuery(id+"F6.wireOp",EDGE,"E492")}),1.0]])]});
            var Q11;
            Q11=makeQuery(id+"F6.imprint","IMPRINT",FACE,{"disambiguationData":[TD([[makeQuery(id+"F6.imprint","IMPRINT",EDGE,{"derivedFrom":sQuery(id+"F6.wireOp",EDGE,"E487")}),1.0]])]});
            var Q12;
            Q12=makeQuery(id+"F6.imprint","IMPRINT",FACE,{"disambiguationData":[TD([[makeQuery(id+"F6.imprint","IMPRINT",EDGE,{"derivedFrom":sQuery(id+"F6.wireOp",EDGE,"E483")}),1.0]])]});
            var Q13;
            Q13=makeQuery(id+"F6.imprint","IMPRINT",FACE,{"disambiguationData":[TD([[makeQuery(id+"F6.imprint","IMPRINT",EDGE,{"derivedFrom":sQuery(id+"F6.wireOp",EDGE,"E468")}),1.0]])]});
            var Q14;
            Q14=makeQuery(id+"F6.imprint","IMPRINT",FACE,{"disambiguationData":[TD([[makeQuery(id+"F6.imprint","IMPRINT",EDGE,{"derivedFrom":sQuery(id+"F6.wireOp",EDGE,"E467")}),1.0]])]});
            var Q15;
            Q15=makeQuery(id+"F6.imprint","IMPRINT",FACE,{"disambiguationData":[TD([[makeQuery(id+"F6.imprint","IMPRINT",EDGE,{"derivedFrom":sQuery(id+"F6.wireOp",EDGE,"E469")}),1.0]])]});
            extrude(context, id + "F7", {"entities" : qUnion([Q0, Q1, Q2, Q3, Q4, Q5, Q6, Q7, Q8, Q9, Q10, Q11, Q12, Q13, Q14, Q15]), "operationType" : NewBodyOperationType.REMOVE, "oppositeDirection" : true, "depth" : 25 * mm});
        }
    });
